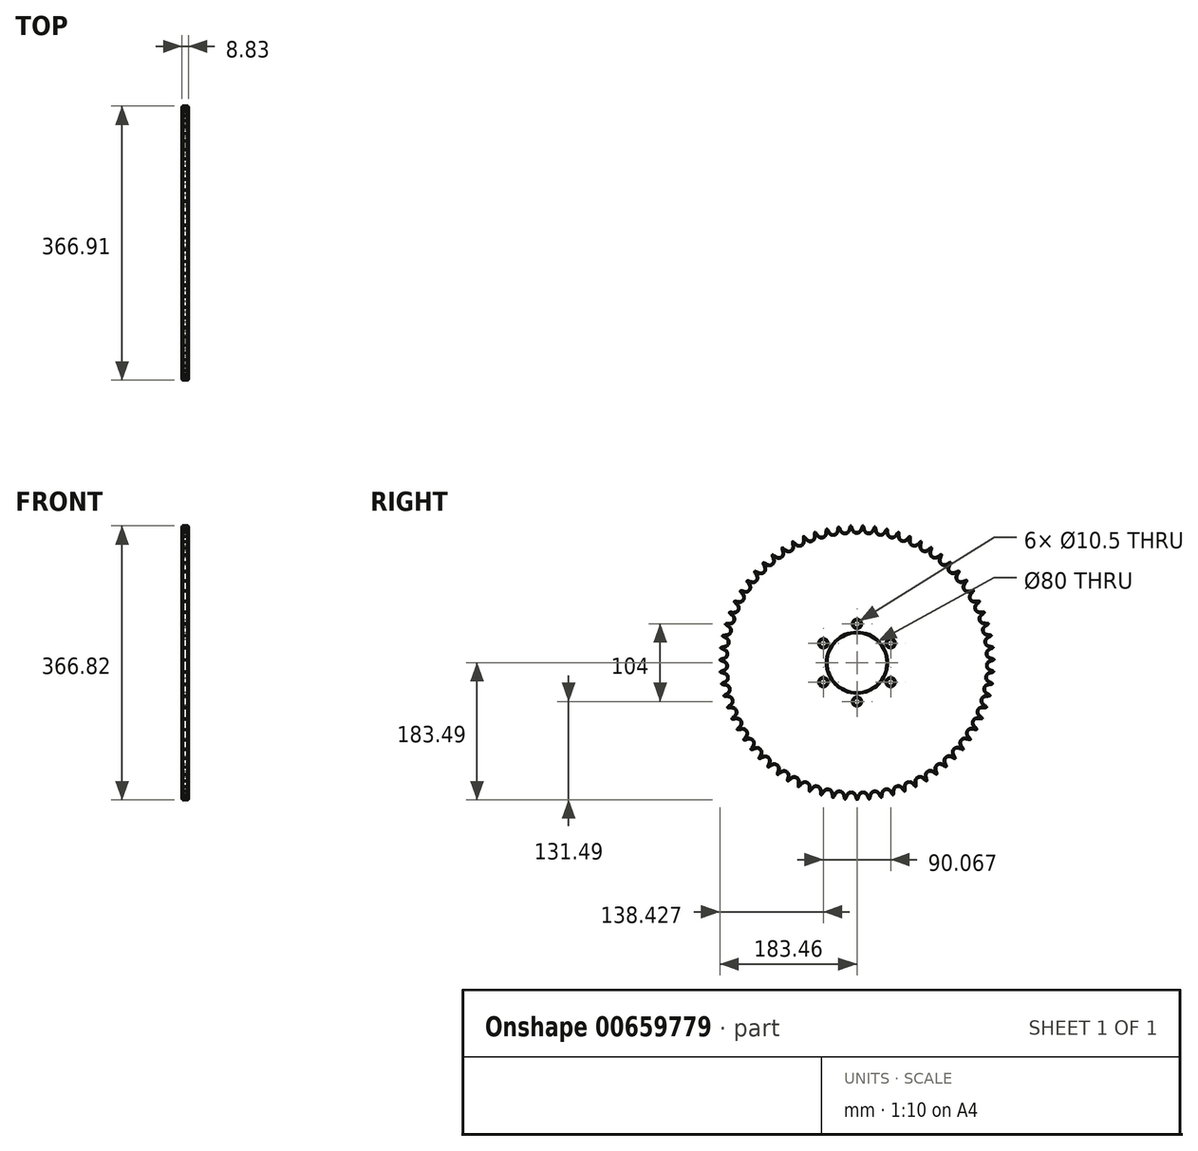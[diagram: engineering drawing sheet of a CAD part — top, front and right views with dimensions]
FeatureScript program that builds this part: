
annotation { "Feature Type Name" : "Feature", "Feature Type Description" : "" }
export const myFeature = defineFeature(function(context is Context, id is Id, definition is map)
    precondition{}
    {
        {
            var Q0;
            Q0=qCreatedBy(makeId("Front.planeOp"),FACE);
            var sketch = newSketch(context, id + "F0", { "sketchPlane" : qUnion([Q0])});
            skLineSegment(sketch, "E0", {"start": v(0, 0) * mm, "end": v(26.72, 0) * mm, "construction": true});
            skLineSegment(sketch, "E1.bottom", {"start": v(0, 40) * mm, "end": v(8.83, 40) * mm});
            skLineSegment(sketch, "E1.top", {"start": v(0, 183.5) * mm, "end": v(8.83, 183.5) * mm});
            skLineSegment(sketch, "E1.left", {"start": v(0, 40) * mm, "end": v(0, 183.5) * mm});
            skLineSegment(sketch, "E1.right", {"start": v(8.83, 40) * mm, "end": v(8.82, 183.5) * mm});
            skLineSegment(sketch, "E2.MirrorCS", {"start": v(8.83, -40) * mm, "end": v(8.83, -183.5) * mm});
            skLineSegment(sketch, "E3.MirrorCS", {"start": v(0, -183.5) * mm, "end": v(8.83, -183.5) * mm});
            skLineSegment(sketch, "E4.MirrorCS", {"start": v(0, -40) * mm, "end": v(8.83, -40) * mm});
            skLineSegment(sketch, "E5.MirrorCS", {"start": v(0, -40) * mm, "end": v(0, -183.5) * mm});
            skSolve(sketch);
        }
        {
            var Q0;
            Q0=makeQuery(id+"F0.imprint","IMPRINT",FACE,{"disambiguationData":[TD([[makeQuery(id+"F0.imprint","IMPRINT",EDGE,{"derivedFrom":sQuery(id+"F0.wireOp",EDGE,"E1.bottom")}),1.0]])]});
            var Q1;
            Q1=sQuery(id+"F0.wireOp",EDGE,"E0");
            revolve(context, id + "F1", {"entities" : qUnion([Q0]), "axis" : qUnion([Q1]), "revolveType" : RevolveType.FULL});
        }
        {
            var Q0;
            Q0=makeQuery(id+"F1.opRevolve","SWEPT_FACE",FACE,{"disambiguationData":[OSD([sQuery(id+"F0.wireOp",EDGE,"E1.left")])]});
            var sketch = newSketch(context, id + "F2", { "sketchPlane" : qUnion([Q0])});
            skCircle(sketch, "E6", {"center": v(0.24, 0) * mm, "radius": 183.5 * mm, "construction": true});
            skCircle(sketch, "E7", {"center": v(0.24, 0) * mm, "radius": 179.5 * mm, "construction": true});
            skCircle(sketch, "E8", {"center": v(0.24, 0) * mm, "radius": 174.3 * mm, "construction": true});
            skLineSegment(sketch, "E9", {"start": v(0.24, 0) * mm, "end": v(0.24, 107.73) * mm, "construction": true});
            skLineSegment(sketch, "E10", {"start": v(-3.61, 87) * mm, "end": v(0.24, 0) * mm, "construction": true});
            skLineSegment(sketch, "E11", {"start": v(0, 0) * mm, "end": v(0, 107.73) * mm, "construction": true});
            skLineSegment(sketch, "E12", {"start": v(0, 179.5) * mm, "end": v(-70.73, 128.4) * mm, "construction": true});
            skLineSegment(sketch, "E13", {"start": v(0, 179.5) * mm, "end": v(6.59, 184.25) * mm, "construction": true});
            skLineSegment(sketch, "E14", {"start": v(6.59, 184.25) * mm, "end": v(-48.15, 165.8) * mm, "construction": true});
            skLineSegment(sketch, "E15", {"start": v(-6, 180) * mm, "end": v(-6.35, 181.04) * mm});
            skLineSegment(sketch, "E16", {"start": v(-6.35, 181.04) * mm, "end": v(-12.59, 178.93) * mm, "construction": true});
            skArc(sketch, "E17", {"start": v(-6, 180) * mm, "mid": v(-5.22, 178.17) * mm, "end": v(-4.18, 176.47) * mm});
            skArc(sketch, "E18", {"start": v(-4.18, 176.47) * mm, "mid": v(18.4, 190.33) * mm, "end": v(-6, 180) * mm, "construction": true});
            skArc(sketch, "E19", {"start": v(0, 174.34) * mm, "mid": v(2.35, 184.08) * mm, "end": v(-4.18, 176.47) * mm, "construction": true});
            skArc(sketch, "E20", {"start": v(-4.18, 176.47) * mm, "mid": v(-2.35, 174.9) * mm, "end": v(0, 174.34) * mm});
            skLineSegment(sketch, "E21", {"start": v(0, 174.34) * mm, "end": v(0.24, 174.34) * mm});
            skArc(sketch, "E22", {"start": v(-7.89, 183.55) * mm, "mid": v(-18.2, 175.49) * mm, "end": v(-6.35, 181.04) * mm, "construction": true});
            skArc(sketch, "E23", {"start": v(-6.35, 181.04) * mm, "mid": v(-6.98, 182.38) * mm, "end": v(-7.89, 183.55) * mm});
            skArc(sketch, "E24.MirrorCS", {"start": v(4.65, 176.47) * mm, "mid": v(2.82, 174.9) * mm, "end": v(0.48, 174.34) * mm});
            skArc(sketch, "E25.MirrorCS", {"start": v(6.47, 180) * mm, "mid": v(5.7, 178.17) * mm, "end": v(4.65, 176.47) * mm});
            skLineSegment(sketch, "E26.MirrorCS", {"start": v(6.47, 180) * mm, "end": v(6.82, 181.04) * mm});
            skArc(sketch, "E27.MirrorCS", {"start": v(6.82, 181.04) * mm, "mid": v(7.45, 182.38) * mm, "end": v(8.36, 183.55) * mm});
            skLineSegment(sketch, "E28.MirrorCS", {"start": v(0.48, 174.34) * mm, "end": v(0.24, 174.34) * mm});
            skArc(sketch, "E29.1.0", {"start": v(-22.32, 179.77) * mm, "mid": v(-23.07, 181.05) * mm, "end": v(-24.08, 182.13) * mm});
            skArc(sketch, "E29.1.1", {"start": v(-9.2, 180.93) * mm, "mid": v(-8.7, 182.33) * mm, "end": v(-7.89, 183.57) * mm});
            skLineSegment(sketch, "E29.1.2", {"start": v(-9.46, 179.87) * mm, "end": v(-9.2, 180.93) * mm});
            skArc(sketch, "E29.1.3", {"start": v(-9.46, 179.87) * mm, "mid": v(-10.07, 177.98) * mm, "end": v(-10.96, 176.2) * mm});
            skArc(sketch, "E29.1.4", {"start": v(-10.96, 176.2) * mm, "mid": v(-12.65, 174.47) * mm, "end": v(-14.93, 173.7) * mm});
            skArc(sketch, "E29.1.5", {"start": v(-19.76, 175.41) * mm, "mid": v(-17.8, 174) * mm, "end": v(-15.4, 173.65) * mm});
            skArc(sketch, "E29.1.6", {"start": v(-21.88, 178.77) * mm, "mid": v(-20.95, 177.01) * mm, "end": v(-19.76, 175.41) * mm});
            skLineSegment(sketch, "E29.1.7", {"start": v(-21.88, 178.77) * mm, "end": v(-22.32, 179.77) * mm});
            skLineSegment(sketch, "E29.1.8", {"start": v(-14.93, 173.7) * mm, "end": v(-15.17, 173.67) * mm});
            skLineSegment(sketch, "E29.1.9", {"start": v(-15.4, 173.65) * mm, "end": v(-15.17, 173.67) * mm});
            skArc(sketch, "E29.2.0", {"start": v(-38.12, 177.1) * mm, "mid": v(-38.98, 178.3) * mm, "end": v(-40.08, 179.3) * mm});
            skArc(sketch, "E29.2.1", {"start": v(-25.16, 179.41) * mm, "mid": v(-24.78, 180.84) * mm, "end": v(-24.08, 182.15) * mm});
            skLineSegment(sketch, "E29.2.2", {"start": v(-25.32, 178.33) * mm, "end": v(-25.16, 179.41) * mm});
            skArc(sketch, "E29.2.3", {"start": v(-25.32, 178.33) * mm, "mid": v(-25.76, 176.4) * mm, "end": v(-26.49, 174.53) * mm});
            skArc(sketch, "E29.2.4", {"start": v(-26.49, 174.53) * mm, "mid": v(-28.02, 172.67) * mm, "end": v(-30.23, 171.7) * mm});
            skArc(sketch, "E29.2.5", {"start": v(-35.18, 172.98) * mm, "mid": v(-33.1, 171.76) * mm, "end": v(-30.7, 171.61) * mm});
            skArc(sketch, "E29.2.6", {"start": v(-37.6, 176.14) * mm, "mid": v(-36.51, 174.47) * mm, "end": v(-35.18, 172.98) * mm});
            skLineSegment(sketch, "E29.2.7", {"start": v(-37.6, 176.14) * mm, "end": v(-38.12, 177.1) * mm});
            skLineSegment(sketch, "E29.2.8", {"start": v(-30.23, 171.7) * mm, "end": v(-30.46, 171.65) * mm});
            skLineSegment(sketch, "E29.2.9", {"start": v(-30.7, 171.61) * mm, "end": v(-30.46, 171.65) * mm});
            skArc(sketch, "E29.3.0", {"start": v(-53.62, 173.03) * mm, "mid": v(-54.58, 174.16) * mm, "end": v(-55.77, 175.05) * mm});
            skArc(sketch, "E29.3.1", {"start": v(-40.92, 176.48) * mm, "mid": v(-40.66, 177.95) * mm, "end": v(-40.09, 179.31) * mm});
            skLineSegment(sketch, "E29.3.2", {"start": v(-40.98, 175.4) * mm, "end": v(-40.92, 176.48) * mm});
            skArc(sketch, "E29.3.3", {"start": v(-40.98, 175.4) * mm, "mid": v(-41.25, 173.42) * mm, "end": v(-41.81, 171.51) * mm});
            skArc(sketch, "E29.3.4", {"start": v(-41.81, 171.51) * mm, "mid": v(-43.17, 169.51) * mm, "end": v(-45.28, 168.35) * mm});
            skArc(sketch, "E29.3.5", {"start": v(-50.33, 169.2) * mm, "mid": v(-48.15, 168.16) * mm, "end": v(-45.74, 168.23) * mm});
            skArc(sketch, "E29.3.6", {"start": v(-53.02, 172.13) * mm, "mid": v(-51.79, 170.56) * mm, "end": v(-50.33, 169.2) * mm});
            skLineSegment(sketch, "E29.3.7", {"start": v(-53.02, 172.13) * mm, "end": v(-53.62, 173.03) * mm});
            skLineSegment(sketch, "E29.3.8", {"start": v(-45.28, 168.35) * mm, "end": v(-45.51, 168.3) * mm});
            skLineSegment(sketch, "E29.3.9", {"start": v(-45.74, 168.23) * mm, "end": v(-45.51, 168.3) * mm});
            skArc(sketch, "E29.4.0", {"start": v(-68.7, 167.61) * mm, "mid": v(-69.76, 168.66) * mm, "end": v(-71.02, 169.43) * mm});
            skArc(sketch, "E29.4.1", {"start": v(-56.36, 172.18) * mm, "mid": v(-56.23, 173.66) * mm, "end": v(-55.78, 175.07) * mm});
            skLineSegment(sketch, "E29.4.2", {"start": v(-56.32, 171.1) * mm, "end": v(-56.36, 172.18) * mm});
            skArc(sketch, "E29.4.3", {"start": v(-56.32, 171.1) * mm, "mid": v(-56.42, 169.1) * mm, "end": v(-56.8, 167.14) * mm});
            skArc(sketch, "E29.4.4", {"start": v(-56.8, 167.14) * mm, "mid": v(-57.98, 165.04) * mm, "end": v(-59.98, 163.7) * mm});
            skArc(sketch, "E29.4.5", {"start": v(-65.1, 164.08) * mm, "mid": v(-62.83, 163.24) * mm, "end": v(-60.43, 163.53) * mm});
            skArc(sketch, "E29.4.6", {"start": v(-68.02, 166.77) * mm, "mid": v(-66.66, 165.31) * mm, "end": v(-65.1, 164.08) * mm});
            skLineSegment(sketch, "E29.4.7", {"start": v(-68.02, 166.77) * mm, "end": v(-68.7, 167.61) * mm});
            skLineSegment(sketch, "E29.4.8", {"start": v(-59.98, 163.7) * mm, "end": v(-60.2, 163.6) * mm});
            skLineSegment(sketch, "E29.4.9", {"start": v(-60.43, 163.53) * mm, "end": v(-60.2, 163.6) * mm});
            skArc(sketch, "E29.5.0", {"start": v(-83.25, 160.89) * mm, "mid": v(-84.4, 161.83) * mm, "end": v(-85.72, 162.5) * mm});
            skArc(sketch, "E29.5.1", {"start": v(-71.35, 166.52) * mm, "mid": v(-71.36, 168) * mm, "end": v(-71.03, 169.45) * mm});
            skLineSegment(sketch, "E29.5.2", {"start": v(-71.22, 165.44) * mm, "end": v(-71.35, 166.52) * mm});
            skArc(sketch, "E29.5.3", {"start": v(-71.22, 165.44) * mm, "mid": v(-71.14, 163.45) * mm, "end": v(-71.36, 161.47) * mm});
            skArc(sketch, "E29.5.4", {"start": v(-71.36, 161.47) * mm, "mid": v(-72.34, 159.27) * mm, "end": v(-74.22, 157.75) * mm});
            skArc(sketch, "E29.5.5", {"start": v(-79.34, 157.69) * mm, "mid": v(-77, 157.05) * mm, "end": v(-74.65, 157.55) * mm});
            skArc(sketch, "E29.5.6", {"start": v(-82.5, 160.1) * mm, "mid": v(-81, 158.78) * mm, "end": v(-79.34, 157.69) * mm});
            skLineSegment(sketch, "E29.5.7", {"start": v(-82.5, 160.1) * mm, "end": v(-83.25, 160.89) * mm});
            skLineSegment(sketch, "E29.5.8", {"start": v(-74.22, 157.75) * mm, "end": v(-74.43, 157.65) * mm});
            skLineSegment(sketch, "E29.5.9", {"start": v(-74.65, 157.55) * mm, "end": v(-74.43, 157.65) * mm});
            skArc(sketch, "E29.6.0", {"start": v(-97.14, 152.9) * mm, "mid": v(-98.37, 153.74) * mm, "end": v(-99.75, 154.28) * mm});
            skArc(sketch, "E29.6.1", {"start": v(-85.79, 159.57) * mm, "mid": v(-85.93, 161.04) * mm, "end": v(-85.73, 162.51) * mm});
            skLineSegment(sketch, "E29.6.2", {"start": v(-85.57, 158.5) * mm, "end": v(-85.79, 159.57) * mm});
            skArc(sketch, "E29.6.3", {"start": v(-85.57, 158.5) * mm, "mid": v(-85.3, 156.52) * mm, "end": v(-85.35, 154.53) * mm});
            skArc(sketch, "E29.6.4", {"start": v(-85.35, 154.53) * mm, "mid": v(-86.13, 152.25) * mm, "end": v(-87.87, 150.57) * mm});
            skArc(sketch, "E29.6.5", {"start": v(-92.96, 150.06) * mm, "mid": v(-90.59, 149.63) * mm, "end": v(-88.28, 150.33) * mm});
            skArc(sketch, "E29.6.6", {"start": v(-96.32, 152.18) * mm, "mid": v(-94.72, 151) * mm, "end": v(-92.96, 150.06) * mm});
            skLineSegment(sketch, "E29.6.7", {"start": v(-96.32, 152.18) * mm, "end": v(-97.14, 152.9) * mm});
            skLineSegment(sketch, "E29.6.8", {"start": v(-87.87, 150.57) * mm, "end": v(-88.07, 150.45) * mm});
            skLineSegment(sketch, "E29.6.9", {"start": v(-88.28, 150.33) * mm, "end": v(-88.07, 150.45) * mm});
            skArc(sketch, "E29.7.0", {"start": v(-110.28, 143.71) * mm, "mid": v(-111.57, 144.44) * mm, "end": v(-113, 144.86) * mm});
            skArc(sketch, "E29.7.1", {"start": v(-99.56, 151.36) * mm, "mid": v(-99.82, 152.82) * mm, "end": v(-99.76, 154.3) * mm});
            skLineSegment(sketch, "E29.7.2", {"start": v(-99.24, 150.32) * mm, "end": v(-99.56, 151.36) * mm});
            skArc(sketch, "E29.7.3", {"start": v(-99.24, 150.32) * mm, "mid": v(-98.8, 148.37) * mm, "end": v(-98.67, 146.38) * mm});
            skArc(sketch, "E29.7.4", {"start": v(-98.67, 146.38) * mm, "mid": v(-99.25, 144.04) * mm, "end": v(-100.83, 142.22) * mm});
            skArc(sketch, "E29.7.5", {"start": v(-105.86, 141.26) * mm, "mid": v(-103.46, 141.04) * mm, "end": v(-101.22, 141.94) * mm});
            skArc(sketch, "E29.7.6", {"start": v(-109.4, 143.08) * mm, "mid": v(-107.7, 142.03) * mm, "end": v(-105.86, 141.26) * mm});
            skLineSegment(sketch, "E29.7.7", {"start": v(-109.4, 143.08) * mm, "end": v(-110.28, 143.71) * mm});
            skLineSegment(sketch, "E29.7.8", {"start": v(-100.83, 142.22) * mm, "end": v(-101.03, 142.08) * mm});
            skLineSegment(sketch, "E29.7.9", {"start": v(-101.22, 141.94) * mm, "end": v(-101.03, 142.08) * mm});
            skArc(sketch, "E29.8.0", {"start": v(-122.55, 133.4) * mm, "mid": v(-123.9, 134.02) * mm, "end": v(-125.35, 134.3) * mm});
            skArc(sketch, "E29.8.1", {"start": v(-112.54, 141.97) * mm, "mid": v(-112.94, 143.4) * mm, "end": v(-113, 144.88) * mm});
            skLineSegment(sketch, "E29.8.2", {"start": v(-112.14, 140.96) * mm, "end": v(-112.54, 141.97) * mm});
            skArc(sketch, "E29.8.3", {"start": v(-112.14, 140.96) * mm, "mid": v(-111.53, 139.06) * mm, "end": v(-111.22, 137.1) * mm});
            skArc(sketch, "E29.8.4", {"start": v(-111.22, 137.1) * mm, "mid": v(-111.6, 134.7) * mm, "end": v(-113, 132.75) * mm});
            skArc(sketch, "E29.8.5", {"start": v(-117.93, 131.35) * mm, "mid": v(-115.52, 131.34) * mm, "end": v(-113.37, 132.44) * mm});
            skArc(sketch, "E29.8.6", {"start": v(-121.61, 132.85) * mm, "mid": v(-119.83, 131.96) * mm, "end": v(-117.93, 131.35) * mm});
            skLineSegment(sketch, "E29.8.7", {"start": v(-121.61, 132.85) * mm, "end": v(-122.55, 133.4) * mm});
            skLineSegment(sketch, "E29.8.8", {"start": v(-113, 132.75) * mm, "end": v(-113.19, 132.6) * mm});
            skLineSegment(sketch, "E29.8.9", {"start": v(-113.37, 132.44) * mm, "end": v(-113.19, 132.6) * mm});
            skArc(sketch, "E29.9.0", {"start": v(-133.86, 122.05) * mm, "mid": v(-135.26, 122.54) * mm, "end": v(-136.73, 122.7) * mm});
            skArc(sketch, "E29.9.1", {"start": v(-124.65, 131.47) * mm, "mid": v(-125.17, 132.85) * mm, "end": v(-125.37, 134.33) * mm});
            skLineSegment(sketch, "E29.9.2", {"start": v(-124.16, 130.5) * mm, "end": v(-124.65, 131.47) * mm});
            skArc(sketch, "E29.9.3", {"start": v(-124.16, 130.5) * mm, "mid": v(-123.39, 128.66) * mm, "end": v(-122.9, 126.72) * mm});
            skArc(sketch, "E29.9.4", {"start": v(-122.9, 126.72) * mm, "mid": v(-123.06, 124.32) * mm, "end": v(-124.3, 122.24) * mm});
            skArc(sketch, "E29.9.5", {"start": v(-129.08, 120.4) * mm, "mid": v(-126.67, 120.62) * mm, "end": v(-124.63, 121.9) * mm});
            skArc(sketch, "E29.9.6", {"start": v(-132.88, 121.58) * mm, "mid": v(-131.02, 120.85) * mm, "end": v(-129.08, 120.4) * mm});
            skLineSegment(sketch, "E29.9.7", {"start": v(-132.88, 121.58) * mm, "end": v(-133.86, 122.05) * mm});
            skLineSegment(sketch, "E29.9.8", {"start": v(-124.3, 122.24) * mm, "end": v(-124.46, 122.07) * mm});
            skLineSegment(sketch, "E29.9.9", {"start": v(-124.63, 121.9) * mm, "end": v(-124.46, 122.07) * mm});
            skArc(sketch, "E29.10.0", {"start": v(-144.12, 109.74) * mm, "mid": v(-145.56, 110.1) * mm, "end": v(-147.04, 110.14) * mm});
            skArc(sketch, "E29.10.1", {"start": v(-135.78, 119.93) * mm, "mid": v(-136.42, 121.27) * mm, "end": v(-136.75, 122.72) * mm});
            skLineSegment(sketch, "E29.10.2", {"start": v(-135.2, 119.01) * mm, "end": v(-135.78, 119.93) * mm});
            skArc(sketch, "E29.10.3", {"start": v(-135.2, 119.01) * mm, "mid": v(-134.28, 117.25) * mm, "end": v(-133.62, 115.37) * mm});
            skArc(sketch, "E29.10.4", {"start": v(-133.62, 115.37) * mm, "mid": v(-133.57, 112.95) * mm, "end": v(-134.61, 110.78) * mm});
            skArc(sketch, "E29.10.5", {"start": v(-139.22, 108.53) * mm, "mid": v(-136.84, 108.95) * mm, "end": v(-134.92, 110.41) * mm});
            skArc(sketch, "E29.10.6", {"start": v(-143.1, 109.36) * mm, "mid": v(-141.2, 108.8) * mm, "end": v(-139.22, 108.53) * mm});
            skLineSegment(sketch, "E29.10.7", {"start": v(-143.1, 109.36) * mm, "end": v(-144.12, 109.74) * mm});
            skLineSegment(sketch, "E29.10.8", {"start": v(-134.61, 110.78) * mm, "end": v(-134.77, 110.6) * mm});
            skLineSegment(sketch, "E29.10.9", {"start": v(-134.92, 110.41) * mm, "end": v(-134.77, 110.6) * mm});
            skArc(sketch, "E29.11.0", {"start": v(-153.26, 96.58) * mm, "mid": v(-154.72, 96.81) * mm, "end": v(-156.2, 96.71) * mm});
            skArc(sketch, "E29.11.1", {"start": v(-145.85, 107.46) * mm, "mid": v(-146.6, 108.74) * mm, "end": v(-147.06, 110.15) * mm});
            skLineSegment(sketch, "E29.11.2", {"start": v(-145.2, 106.6) * mm, "end": v(-145.85, 107.46) * mm});
            skArc(sketch, "E29.11.3", {"start": v(-145.2, 106.6) * mm, "mid": v(-144.11, 104.92) * mm, "end": v(-143.3, 103.1) * mm});
            skArc(sketch, "E29.11.4", {"start": v(-143.3, 103.1) * mm, "mid": v(-143.03, 100.7) * mm, "end": v(-143.88, 98.45) * mm});
            skArc(sketch, "E29.11.5", {"start": v(-148.26, 95.8) * mm, "mid": v(-145.93, 96.43) * mm, "end": v(-144.15, 98.06) * mm});
            skArc(sketch, "E29.11.6", {"start": v(-152.2, 96.29) * mm, "mid": v(-150.25, 95.9) * mm, "end": v(-148.26, 95.8) * mm});
            skLineSegment(sketch, "E29.11.7", {"start": v(-152.2, 96.29) * mm, "end": v(-153.26, 96.58) * mm});
            skLineSegment(sketch, "E29.11.8", {"start": v(-143.88, 98.45) * mm, "end": v(-144.01, 98.25) * mm});
            skLineSegment(sketch, "E29.11.9", {"start": v(-144.15, 98.06) * mm, "end": v(-144.01, 98.25) * mm});
            skArc(sketch, "E29.12.0", {"start": v(-161.2, 82.65) * mm, "mid": v(-162.67, 82.76) * mm, "end": v(-164.14, 82.53) * mm});
            skArc(sketch, "E29.12.1", {"start": v(-154.78, 94.15) * mm, "mid": v(-155.64, 95.36) * mm, "end": v(-156.22, 96.73) * mm});
            skLineSegment(sketch, "E29.12.2", {"start": v(-154.05, 93.35) * mm, "end": v(-154.78, 94.15) * mm});
            skArc(sketch, "E29.12.3", {"start": v(-154.05, 93.35) * mm, "mid": v(-152.82, 91.78) * mm, "end": v(-151.85, 90.04) * mm});
            skArc(sketch, "E29.12.4", {"start": v(-151.85, 90.04) * mm, "mid": v(-151.37, 87.67) * mm, "end": v(-152.02, 85.35) * mm});
            skArc(sketch, "E29.12.5", {"start": v(-156.15, 82.32) * mm, "mid": v(-153.89, 83.16) * mm, "end": v(-152.25, 84.93) * mm});
            skArc(sketch, "E29.12.6", {"start": v(-160.12, 82.46) * mm, "mid": v(-158.14, 82.24) * mm, "end": v(-156.15, 82.32) * mm});
            skLineSegment(sketch, "E29.12.7", {"start": v(-160.12, 82.46) * mm, "end": v(-161.2, 82.65) * mm});
            skLineSegment(sketch, "E29.12.8", {"start": v(-152.02, 85.35) * mm, "end": v(-152.13, 85.14) * mm});
            skLineSegment(sketch, "E29.12.9", {"start": v(-152.25, 84.93) * mm, "end": v(-152.13, 85.14) * mm});
            skArc(sketch, "E29.13.0", {"start": v(-167.87, 68.09) * mm, "mid": v(-169.35, 68.06) * mm, "end": v(-170.79, 67.7) * mm});
            skArc(sketch, "E29.13.1", {"start": v(-162.5, 80.1) * mm, "mid": v(-163.46, 81.23) * mm, "end": v(-164.16, 82.54) * mm});
            skLineSegment(sketch, "E29.13.2", {"start": v(-161.7, 79.37) * mm, "end": v(-162.5, 80.1) * mm});
            skArc(sketch, "E29.13.3", {"start": v(-161.7, 79.37) * mm, "mid": v(-160.34, 77.9) * mm, "end": v(-159.2, 76.26) * mm});
            skArc(sketch, "E29.13.4", {"start": v(-159.2, 76.26) * mm, "mid": v(-158.52, 73.95) * mm, "end": v(-158.96, 71.58) * mm});
            skArc(sketch, "E29.13.5", {"start": v(-162.81, 68.2) * mm, "mid": v(-160.63, 69.23) * mm, "end": v(-159.16, 71.14) * mm});
            skArc(sketch, "E29.13.6", {"start": v(-166.78, 67.98) * mm, "mid": v(-164.8, 67.94) * mm, "end": v(-162.81, 68.2) * mm});
            skLineSegment(sketch, "E29.13.7", {"start": v(-166.78, 67.98) * mm, "end": v(-167.87, 68.09) * mm});
            skLineSegment(sketch, "E29.13.8", {"start": v(-158.96, 71.58) * mm, "end": v(-159.06, 71.36) * mm});
            skLineSegment(sketch, "E29.13.9", {"start": v(-159.16, 71.14) * mm, "end": v(-159.06, 71.36) * mm});
            skArc(sketch, "E29.14.0", {"start": v(-173.23, 52.98) * mm, "mid": v(-174.7, 52.83) * mm, "end": v(-176.1, 52.34) * mm});
            skArc(sketch, "E29.14.1", {"start": v(-168.94, 65.43) * mm, "mid": v(-170, 66.46) * mm, "end": v(-170.8, 67.7) * mm});
            skLineSegment(sketch, "E29.14.2", {"start": v(-168.08, 64.77) * mm, "end": v(-168.94, 65.43) * mm});
            skArc(sketch, "E29.14.3", {"start": v(-168.08, 64.77) * mm, "mid": v(-166.6, 63.43) * mm, "end": v(-165.33, 61.9) * mm});
            skArc(sketch, "E29.14.4", {"start": v(-165.33, 61.9) * mm, "mid": v(-164.44, 59.65) * mm, "end": v(-164.67, 57.25) * mm});
            skArc(sketch, "E29.14.5", {"start": v(-168.2, 53.54) * mm, "mid": v(-166.12, 54.76) * mm, "end": v(-164.82, 56.8) * mm});
            skArc(sketch, "E29.14.6", {"start": v(-172.14, 52.98) * mm, "mid": v(-170.15, 53.11) * mm, "end": v(-168.2, 53.54) * mm});
            skLineSegment(sketch, "E29.14.7", {"start": v(-172.14, 52.98) * mm, "end": v(-173.23, 52.98) * mm});
            skLineSegment(sketch, "E29.14.8", {"start": v(-164.67, 57.25) * mm, "end": v(-164.75, 57.02) * mm});
            skLineSegment(sketch, "E29.14.9", {"start": v(-164.82, 56.8) * mm, "end": v(-164.75, 57.02) * mm});
            skArc(sketch, "E29.15.0", {"start": v(-177.23, 37.47) * mm, "mid": v(-178.69, 37.18) * mm, "end": v(-180.04, 36.57) * mm});
            skArc(sketch, "E29.15.1", {"start": v(-174.06, 50.24) * mm, "mid": v(-175.21, 51.18) * mm, "end": v(-176.12, 52.35) * mm});
            skLineSegment(sketch, "E29.15.2", {"start": v(-173.14, 49.66) * mm, "end": v(-174.06, 50.24) * mm});
            skArc(sketch, "E29.15.3", {"start": v(-173.14, 49.66) * mm, "mid": v(-171.55, 48.46) * mm, "end": v(-170.15, 47.04) * mm});
            skArc(sketch, "E29.15.4", {"start": v(-170.15, 47.04) * mm, "mid": v(-169.07, 44.88) * mm, "end": v(-169.08, 42.47) * mm});
            skArc(sketch, "E29.15.5", {"start": v(-172.28, 38.47) * mm, "mid": v(-170.31, 39.87) * mm, "end": v(-169.2, 42) * mm});
            skArc(sketch, "E29.15.6", {"start": v(-176.15, 37.55) * mm, "mid": v(-174.18, 37.87) * mm, "end": v(-172.28, 38.47) * mm});
            skLineSegment(sketch, "E29.15.7", {"start": v(-176.15, 37.55) * mm, "end": v(-177.23, 37.47) * mm});
            skLineSegment(sketch, "E29.15.8", {"start": v(-169.08, 42.47) * mm, "end": v(-169.14, 42.24) * mm});
            skLineSegment(sketch, "E29.15.9", {"start": v(-169.2, 42) * mm, "end": v(-169.14, 42.24) * mm});
            skArc(sketch, "E29.16.0", {"start": v(-179.85, 21.66) * mm, "mid": v(-181.27, 21.24) * mm, "end": v(-182.57, 20.52) * mm});
            skArc(sketch, "E29.16.1", {"start": v(-177.82, 34.66) * mm, "mid": v(-179.05, 35.5) * mm, "end": v(-180.06, 36.58) * mm});
            skLineSegment(sketch, "E29.16.2", {"start": v(-176.85, 34.16) * mm, "end": v(-177.82, 34.66) * mm});
            skArc(sketch, "E29.16.3", {"start": v(-176.85, 34.16) * mm, "mid": v(-175.16, 33.11) * mm, "end": v(-173.64, 31.82) * mm});
            skArc(sketch, "E29.16.4", {"start": v(-173.64, 31.82) * mm, "mid": v(-172.37, 29.77) * mm, "end": v(-172.18, 27.36) * mm});
            skArc(sketch, "E29.16.5", {"start": v(-175, 23.1) * mm, "mid": v(-173.17, 24.66) * mm, "end": v(-172.25, 26.9) * mm});
            skArc(sketch, "E29.16.6", {"start": v(-178.78, 21.84) * mm, "mid": v(-176.84, 22.32) * mm, "end": v(-175, 23.1) * mm});
            skLineSegment(sketch, "E29.16.7", {"start": v(-178.78, 21.84) * mm, "end": v(-179.85, 21.66) * mm});
            skLineSegment(sketch, "E29.16.8", {"start": v(-172.18, 27.36) * mm, "end": v(-172.21, 27.13) * mm});
            skLineSegment(sketch, "E29.16.9", {"start": v(-172.25, 26.9) * mm, "end": v(-172.21, 27.13) * mm});
            skArc(sketch, "E29.17.0", {"start": v(-181.06, 5.68) * mm, "mid": v(-182.44, 5.14) * mm, "end": v(-183.67, 4.3) * mm});
            skArc(sketch, "E29.17.1", {"start": v(-180.19, 18.81) * mm, "mid": v(-181.48, 19.53) * mm, "end": v(-182.6, 20.52) * mm});
            skLineSegment(sketch, "E29.17.2", {"start": v(-179.18, 18.4) * mm, "end": v(-180.19, 18.81) * mm});
            skArc(sketch, "E29.17.3", {"start": v(-179.18, 18.4) * mm, "mid": v(-177.4, 17.5) * mm, "end": v(-175.77, 16.35) * mm});
            skArc(sketch, "E29.17.4", {"start": v(-175.77, 16.35) * mm, "mid": v(-174.33, 14.42) * mm, "end": v(-173.92, 12.04) * mm});
            skArc(sketch, "E29.17.5", {"start": v(-176.36, 7.53) * mm, "mid": v(-174.67, 9.26) * mm, "end": v(-173.95, 11.56) * mm});
            skArc(sketch, "E29.17.6", {"start": v(-180, 5.95) * mm, "mid": v(-178.12, 6.6) * mm, "end": v(-176.36, 7.53) * mm});
            skLineSegment(sketch, "E29.17.7", {"start": v(-180, 5.95) * mm, "end": v(-181.06, 5.68) * mm});
            skLineSegment(sketch, "E29.17.8", {"start": v(-173.92, 12.04) * mm, "end": v(-173.94, 11.8) * mm});
            skLineSegment(sketch, "E29.17.9", {"start": v(-173.95, 11.56) * mm, "end": v(-173.94, 11.8) * mm});
            skArc(sketch, "E29.18.0", {"start": v(-180.85, -10.35) * mm, "mid": v(-182.18, -11) * mm, "end": v(-183.33, -11.95) * mm});
            skArc(sketch, "E29.18.1", {"start": v(-181.14, 2.82) * mm, "mid": v(-182.5, 3.41) * mm, "end": v(-183.69, 4.3) * mm});
            skLineSegment(sketch, "E29.18.2", {"start": v(-180.1, 2.5) * mm, "end": v(-181.14, 2.82) * mm});
            skArc(sketch, "E29.18.3", {"start": v(-180.1, 2.5) * mm, "mid": v(-178.25, 1.75) * mm, "end": v(-176.53, 0.75) * mm});
            skArc(sketch, "E29.18.4", {"start": v(-176.53, 0.75) * mm, "mid": v(-174.92, -1.05) * mm, "end": v(-174.3, -3.38) * mm});
            skArc(sketch, "E29.18.5", {"start": v(-176.34, -8.08) * mm, "mid": v(-174.8, -6.22) * mm, "end": v(-174.3, -3.86) * mm});
            skArc(sketch, "E29.18.6", {"start": v(-179.83, -9.98) * mm, "mid": v(-178.01, -9.16) * mm, "end": v(-176.34, -8.08) * mm});
            skLineSegment(sketch, "E29.18.7", {"start": v(-179.83, -9.98) * mm, "end": v(-180.85, -10.35) * mm});
            skLineSegment(sketch, "E29.18.8", {"start": v(-174.3, -3.38) * mm, "end": v(-174.3, -3.62) * mm});
            skLineSegment(sketch, "E29.18.9", {"start": v(-174.3, -3.86) * mm, "end": v(-174.3, -3.62) * mm});
            skArc(sketch, "E29.19.0", {"start": v(-179.23, -26.3) * mm, "mid": v(-180.5, -27.07) * mm, "end": v(-181.56, -28.1) * mm});
            skArc(sketch, "E29.19.1", {"start": v(-180.68, -13.2) * mm, "mid": v(-182.09, -12.73) * mm, "end": v(-183.35, -11.95) * mm});
            skLineSegment(sketch, "E29.19.2", {"start": v(-179.62, -13.44) * mm, "end": v(-180.68, -13.2) * mm});
            skArc(sketch, "E29.19.3", {"start": v(-179.62, -13.44) * mm, "mid": v(-177.71, -14) * mm, "end": v(-175.9, -14.86) * mm});
            skArc(sketch, "E29.19.4", {"start": v(-175.9, -14.86) * mm, "mid": v(-174.14, -16.5) * mm, "end": v(-173.32, -18.77) * mm});
            skArc(sketch, "E29.19.5", {"start": v(-174.93, -23.63) * mm, "mid": v(-173.57, -21.64) * mm, "end": v(-173.27, -19.25) * mm});
            skArc(sketch, "E29.19.6", {"start": v(-178.24, -25.83) * mm, "mid": v(-176.5, -24.86) * mm, "end": v(-174.93, -23.63) * mm});
            skLineSegment(sketch, "E29.19.7", {"start": v(-178.24, -25.83) * mm, "end": v(-179.23, -26.3) * mm});
            skLineSegment(sketch, "E29.19.8", {"start": v(-173.32, -18.77) * mm, "end": v(-173.3, -19) * mm});
            skLineSegment(sketch, "E29.19.9", {"start": v(-173.27, -19.25) * mm, "end": v(-173.3, -19) * mm});
            skArc(sketch, "E29.20.0", {"start": v(-176.2, -42.03) * mm, "mid": v(-177.4, -42.91) * mm, "end": v(-178.36, -44.04) * mm});
            skArc(sketch, "E29.20.1", {"start": v(-178.8, -29.12) * mm, "mid": v(-180.25, -28.77) * mm, "end": v(-181.58, -28.1) * mm});
            skLineSegment(sketch, "E29.20.2", {"start": v(-177.73, -29.26) * mm, "end": v(-178.8, -29.12) * mm});
            skArc(sketch, "E29.20.3", {"start": v(-177.73, -29.26) * mm, "mid": v(-175.78, -29.66) * mm, "end": v(-173.9, -30.34) * mm});
            skArc(sketch, "E29.20.4", {"start": v(-173.9, -30.34) * mm, "mid": v(-172, -31.83) * mm, "end": v(-170.99, -34.02) * mm});
            skArc(sketch, "E29.20.5", {"start": v(-172.16, -39) * mm, "mid": v(-170.98, -36.9) * mm, "end": v(-170.9, -34.48) * mm});
            skArc(sketch, "E29.20.6", {"start": v(-175.26, -41.49) * mm, "mid": v(-173.62, -40.36) * mm, "end": v(-172.16, -39) * mm});
            skLineSegment(sketch, "E29.20.7", {"start": v(-175.26, -41.49) * mm, "end": v(-176.2, -42.03) * mm});
            skLineSegment(sketch, "E29.20.8", {"start": v(-170.99, -34.02) * mm, "end": v(-170.94, -34.25) * mm});
            skLineSegment(sketch, "E29.20.9", {"start": v(-170.9, -34.48) * mm, "end": v(-170.94, -34.25) * mm});
            skArc(sketch, "E29.21.0", {"start": v(-171.8, -57.44) * mm, "mid": v(-172.91, -58.42) * mm, "end": v(-173.77, -59.63) * mm});
            skArc(sketch, "E29.21.1", {"start": v(-175.54, -44.81) * mm, "mid": v(-177, -44.59) * mm, "end": v(-178.38, -44.04) * mm});
            skLineSegment(sketch, "E29.21.2", {"start": v(-174.45, -44.85) * mm, "end": v(-175.54, -44.81) * mm});
            skArc(sketch, "E29.21.3", {"start": v(-174.45, -44.85) * mm, "mid": v(-172.47, -45.08) * mm, "end": v(-170.54, -45.6) * mm});
            skArc(sketch, "E29.21.4", {"start": v(-170.54, -45.6) * mm, "mid": v(-168.52, -46.9) * mm, "end": v(-167.3, -49) * mm});
            skArc(sketch, "E29.21.5", {"start": v(-168.04, -54.07) * mm, "mid": v(-167.05, -51.86) * mm, "end": v(-167.17, -49.45) * mm});
            skArc(sketch, "E29.21.6", {"start": v(-170.91, -56.81) * mm, "mid": v(-169.37, -55.55) * mm, "end": v(-168.04, -54.07) * mm});
            skLineSegment(sketch, "E29.21.7", {"start": v(-170.91, -56.81) * mm, "end": v(-171.8, -57.44) * mm});
            skLineSegment(sketch, "E29.21.8", {"start": v(-167.3, -49) * mm, "end": v(-167.24, -49.22) * mm});
            skLineSegment(sketch, "E29.21.9", {"start": v(-167.17, -49.45) * mm, "end": v(-167.24, -49.22) * mm});
            skArc(sketch, "E29.22.0", {"start": v(-166.05, -72.4) * mm, "mid": v(-167.07, -73.48) * mm, "end": v(-167.82, -74.76) * mm});
            skArc(sketch, "E29.22.1", {"start": v(-170.89, -60.15) * mm, "mid": v(-172.37, -60.06) * mm, "end": v(-173.8, -59.64) * mm});
            skLineSegment(sketch, "E29.22.2", {"start": v(-169.8, -60.1) * mm, "end": v(-170.89, -60.15) * mm});
            skArc(sketch, "E29.22.3", {"start": v(-169.8, -60.1) * mm, "mid": v(-167.8, -60.14) * mm, "end": v(-165.85, -60.49) * mm});
            skArc(sketch, "E29.22.4", {"start": v(-165.85, -60.49) * mm, "mid": v(-163.71, -61.62) * mm, "end": v(-162.32, -63.6) * mm});
            skArc(sketch, "E29.22.5", {"start": v(-162.6, -68.7) * mm, "mid": v(-161.81, -66.42) * mm, "end": v(-162.15, -64.03) * mm});
            skArc(sketch, "E29.22.6", {"start": v(-165.22, -71.7) * mm, "mid": v(-163.8, -70.3) * mm, "end": v(-162.6, -68.7) * mm});
            skLineSegment(sketch, "E29.22.7", {"start": v(-165.22, -71.7) * mm, "end": v(-166.05, -72.4) * mm});
            skLineSegment(sketch, "E29.22.8", {"start": v(-162.32, -63.6) * mm, "end": v(-162.24, -63.81) * mm});
            skLineSegment(sketch, "E29.22.9", {"start": v(-162.15, -64.03) * mm, "end": v(-162.24, -63.81) * mm});
            skArc(sketch, "E29.23.0", {"start": v(-159, -86.79) * mm, "mid": v(-159.92, -87.95) * mm, "end": v(-160.56, -89.3) * mm});
            skArc(sketch, "E29.23.1", {"start": v(-164.9, -75.02) * mm, "mid": v(-166.39, -75.06) * mm, "end": v(-167.84, -74.76) * mm});
            skLineSegment(sketch, "E29.23.2", {"start": v(-163.83, -74.87) * mm, "end": v(-164.9, -75.02) * mm});
            skArc(sketch, "E29.23.3", {"start": v(-163.83, -74.87) * mm, "mid": v(-161.84, -74.74) * mm, "end": v(-159.85, -74.91) * mm});
            skArc(sketch, "E29.23.4", {"start": v(-159.85, -74.91) * mm, "mid": v(-157.63, -75.84) * mm, "end": v(-156.07, -77.69) * mm});
            skArc(sketch, "E29.23.5", {"start": v(-155.9, -82.8) * mm, "mid": v(-155.3, -80.47) * mm, "end": v(-155.86, -78.11) * mm});
            skArc(sketch, "E29.23.6", {"start": v(-158.24, -86.02) * mm, "mid": v(-156.95, -84.5) * mm, "end": v(-155.9, -82.8) * mm});
            skLineSegment(sketch, "E29.23.7", {"start": v(-158.24, -86.02) * mm, "end": v(-159, -86.79) * mm});
            skLineSegment(sketch, "E29.23.8", {"start": v(-156.07, -77.69) * mm, "end": v(-155.96, -77.9) * mm});
            skLineSegment(sketch, "E29.23.9", {"start": v(-155.86, -78.11) * mm, "end": v(-155.96, -77.9) * mm});
            skArc(sketch, "E29.24.0", {"start": v(-150.71, -100.5) * mm, "mid": v(-151.52, -101.74) * mm, "end": v(-152.04, -103.14) * mm});
            skArc(sketch, "E29.24.1", {"start": v(-157.63, -89.3) * mm, "mid": v(-159.1, -89.47) * mm, "end": v(-160.58, -89.3) * mm});
            skLineSegment(sketch, "E29.24.2", {"start": v(-156.57, -89.05) * mm, "end": v(-157.63, -89.3) * mm});
            skArc(sketch, "E29.24.3", {"start": v(-156.57, -89.05) * mm, "mid": v(-154.6, -88.75) * mm, "end": v(-152.6, -88.74) * mm});
            skArc(sketch, "E29.24.4", {"start": v(-152.6, -88.74) * mm, "mid": v(-150.3, -89.48) * mm, "end": v(-148.6, -91.18) * mm});
            skArc(sketch, "E29.24.5", {"start": v(-147.97, -96.26) * mm, "mid": v(-147.6, -93.88) * mm, "end": v(-148.34, -91.58) * mm});
            skArc(sketch, "E29.24.6", {"start": v(-150.02, -99.67) * mm, "mid": v(-148.86, -98.04) * mm, "end": v(-147.97, -96.26) * mm});
            skLineSegment(sketch, "E29.24.7", {"start": v(-150.02, -99.67) * mm, "end": v(-150.71, -100.5) * mm});
            skLineSegment(sketch, "E29.24.8", {"start": v(-148.6, -91.18) * mm, "end": v(-148.47, -91.38) * mm});
            skLineSegment(sketch, "E29.24.9", {"start": v(-148.34, -91.58) * mm, "end": v(-148.47, -91.38) * mm});
            skArc(sketch, "E29.25.0", {"start": v(-141.24, -113.43) * mm, "mid": v(-141.94, -114.74) * mm, "end": v(-142.33, -116.17) * mm});
            skArc(sketch, "E29.25.1", {"start": v(-149.12, -102.88) * mm, "mid": v(-150.57, -103.18) * mm, "end": v(-152.06, -103.15) * mm});
            skLineSegment(sketch, "E29.25.2", {"start": v(-148.09, -102.54) * mm, "end": v(-149.12, -102.88) * mm});
            skArc(sketch, "E29.25.3", {"start": v(-148.09, -102.54) * mm, "mid": v(-146.15, -102.07) * mm, "end": v(-144.17, -101.88) * mm});
            skArc(sketch, "E29.25.4", {"start": v(-144.17, -101.88) * mm, "mid": v(-141.8, -102.41) * mm, "end": v(-139.95, -103.95) * mm});
            skArc(sketch, "E29.25.5", {"start": v(-138.88, -108.96) * mm, "mid": v(-138.72, -106.55) * mm, "end": v(-139.67, -104.34) * mm});
            skArc(sketch, "E29.25.6", {"start": v(-140.62, -112.53) * mm, "mid": v(-139.62, -110.81) * mm, "end": v(-138.88, -108.96) * mm});
            skLineSegment(sketch, "E29.25.7", {"start": v(-140.62, -112.53) * mm, "end": v(-141.24, -113.43) * mm});
            skLineSegment(sketch, "E29.25.8", {"start": v(-139.95, -103.95) * mm, "end": v(-139.81, -104.14) * mm});
            skLineSegment(sketch, "E29.25.9", {"start": v(-139.67, -104.34) * mm, "end": v(-139.81, -104.14) * mm});
            skArc(sketch, "E29.26.0", {"start": v(-130.66, -125.47) * mm, "mid": v(-131.24, -126.83) * mm, "end": v(-131.5, -128.3) * mm});
            skArc(sketch, "E29.26.1", {"start": v(-139.44, -115.66) * mm, "mid": v(-140.86, -116.08) * mm, "end": v(-142.34, -116.18) * mm});
            skLineSegment(sketch, "E29.26.2", {"start": v(-138.44, -115.23) * mm, "end": v(-139.44, -115.66) * mm});
            skArc(sketch, "E29.26.3", {"start": v(-138.44, -115.23) * mm, "mid": v(-136.56, -114.58) * mm, "end": v(-134.6, -114.23) * mm});
            skArc(sketch, "E29.26.4", {"start": v(-134.6, -114.23) * mm, "mid": v(-132.2, -114.54) * mm, "end": v(-130.22, -115.92) * mm});
            skArc(sketch, "E29.26.5", {"start": v(-128.7, -120.8) * mm, "mid": v(-128.76, -118.4) * mm, "end": v(-129.9, -116.27) * mm});
            skArc(sketch, "E29.26.6", {"start": v(-130.13, -124.52) * mm, "mid": v(-129.28, -122.72) * mm, "end": v(-128.7, -120.8) * mm});
            skLineSegment(sketch, "E29.26.7", {"start": v(-130.13, -124.52) * mm, "end": v(-130.66, -125.47) * mm});
            skLineSegment(sketch, "E29.26.8", {"start": v(-130.22, -115.92) * mm, "end": v(-130.06, -116.1) * mm});
            skLineSegment(sketch, "E29.26.9", {"start": v(-129.9, -116.27) * mm, "end": v(-130.06, -116.1) * mm});
            skArc(sketch, "E29.27.0", {"start": v(-119.06, -136.53) * mm, "mid": v(-119.52, -137.94) * mm, "end": v(-119.65, -139.41) * mm});
            skArc(sketch, "E29.27.1", {"start": v(-128.68, -127.53) * mm, "mid": v(-130.05, -128.08) * mm, "end": v(-131.52, -128.3) * mm});
            skLineSegment(sketch, "E29.27.2", {"start": v(-127.72, -127.01) * mm, "end": v(-128.68, -127.53) * mm});
            skArc(sketch, "E29.27.3", {"start": v(-127.72, -127.01) * mm, "mid": v(-125.9, -126.2) * mm, "end": v(-123.97, -125.68) * mm});
            skArc(sketch, "E29.27.4", {"start": v(-123.97, -125.68) * mm, "mid": v(-121.56, -125.78) * mm, "end": v(-119.46, -126.97) * mm});
            skArc(sketch, "E29.27.5", {"start": v(-117.52, -131.71) * mm, "mid": v(-117.79, -129.31) * mm, "end": v(-119.12, -127.3) * mm});
            skArc(sketch, "E29.27.6", {"start": v(-118.61, -135.54) * mm, "mid": v(-117.92, -133.66) * mm, "end": v(-117.52, -131.71) * mm});
            skLineSegment(sketch, "E29.27.7", {"start": v(-118.61, -135.54) * mm, "end": v(-119.06, -136.53) * mm});
            skLineSegment(sketch, "E29.27.8", {"start": v(-119.46, -126.97) * mm, "end": v(-119.29, -127.13) * mm});
            skLineSegment(sketch, "E29.27.9", {"start": v(-119.12, -127.3) * mm, "end": v(-119.29, -127.13) * mm});
            skArc(sketch, "E29.28.0", {"start": v(-106.53, -146.51) * mm, "mid": v(-106.86, -147.96) * mm, "end": v(-106.86, -149.44) * mm});
            skArc(sketch, "E29.28.1", {"start": v(-116.9, -138.4) * mm, "mid": v(-118.22, -139.07) * mm, "end": v(-119.66, -139.43) * mm});
            skLineSegment(sketch, "E29.28.2", {"start": v(-116, -137.8) * mm, "end": v(-116.9, -138.4) * mm});
            skArc(sketch, "E29.28.3", {"start": v(-116, -137.8) * mm, "mid": v(-114.25, -136.84) * mm, "end": v(-112.38, -136.14) * mm});
            skArc(sketch, "E29.28.4", {"start": v(-112.38, -136.14) * mm, "mid": v(-109.97, -136.03) * mm, "end": v(-107.77, -137.03) * mm});
            skArc(sketch, "E29.28.5", {"start": v(-105.42, -141.58) * mm, "mid": v(-105.9, -139.22) * mm, "end": v(-107.4, -137.33) * mm});
            skArc(sketch, "E29.28.6", {"start": v(-106.17, -145.49) * mm, "mid": v(-105.65, -143.56) * mm, "end": v(-105.42, -141.58) * mm});
            skLineSegment(sketch, "E29.28.7", {"start": v(-106.17, -145.49) * mm, "end": v(-106.53, -146.51) * mm});
            skLineSegment(sketch, "E29.28.8", {"start": v(-107.77, -137.03) * mm, "end": v(-107.59, -137.18) * mm});
            skLineSegment(sketch, "E29.28.9", {"start": v(-107.4, -137.33) * mm, "end": v(-107.59, -137.18) * mm});
            skArc(sketch, "E29.29.0", {"start": v(-93.16, -155.36) * mm, "mid": v(-93.37, -156.83) * mm, "end": v(-93.23, -158.3) * mm});
            skArc(sketch, "E29.29.1", {"start": v(-104.21, -148.2) * mm, "mid": v(-105.47, -148.98) * mm, "end": v(-106.87, -149.46) * mm});
            skLineSegment(sketch, "E29.29.2", {"start": v(-103.36, -147.52) * mm, "end": v(-104.21, -148.2) * mm});
            skArc(sketch, "E29.29.3", {"start": v(-103.36, -147.52) * mm, "mid": v(-101.7, -146.4) * mm, "end": v(-99.91, -145.54) * mm});
            skArc(sketch, "E29.29.4", {"start": v(-99.91, -145.54) * mm, "mid": v(-97.52, -145.22) * mm, "end": v(-95.24, -146.02) * mm});
            skArc(sketch, "E29.29.5", {"start": v(-92.5, -150.35) * mm, "mid": v(-93.18, -148.03) * mm, "end": v(-94.84, -146.28) * mm});
            skArc(sketch, "E29.29.6", {"start": v(-92.9, -154.3) * mm, "mid": v(-92.55, -152.34) * mm, "end": v(-92.5, -150.35) * mm});
            skLineSegment(sketch, "E29.29.7", {"start": v(-92.9, -154.3) * mm, "end": v(-93.16, -155.36) * mm});
            skLineSegment(sketch, "E29.29.8", {"start": v(-95.24, -146.02) * mm, "end": v(-95.04, -146.15) * mm});
            skLineSegment(sketch, "E29.29.9", {"start": v(-94.84, -146.28) * mm, "end": v(-95.04, -146.15) * mm});
            skArc(sketch, "E29.30.0", {"start": v(-79.07, -162.98) * mm, "mid": v(-79.14, -164.46) * mm, "end": v(-78.88, -165.92) * mm});
            skArc(sketch, "E29.30.1", {"start": v(-90.7, -156.82) * mm, "mid": v(-91.9, -157.72) * mm, "end": v(-93.25, -158.32) * mm});
            skLineSegment(sketch, "E29.30.2", {"start": v(-89.92, -156.07) * mm, "end": v(-90.7, -156.82) * mm});
            skArc(sketch, "E29.30.3", {"start": v(-89.92, -156.07) * mm, "mid": v(-88.37, -154.81) * mm, "end": v(-86.66, -153.8) * mm});
            skArc(sketch, "E29.30.4", {"start": v(-86.66, -153.8) * mm, "mid": v(-84.3, -153.27) * mm, "end": v(-81.96, -153.87) * mm});
            skArc(sketch, "E29.30.5", {"start": v(-78.85, -157.93) * mm, "mid": v(-79.73, -155.69) * mm, "end": v(-81.54, -154.1) * mm});
            skArc(sketch, "E29.30.6", {"start": v(-78.9, -161.9) * mm, "mid": v(-78.72, -159.92) * mm, "end": v(-78.85, -157.93) * mm});
            skLineSegment(sketch, "E29.30.7", {"start": v(-78.9, -161.9) * mm, "end": v(-79.07, -162.98) * mm});
            skLineSegment(sketch, "E29.30.8", {"start": v(-81.96, -153.87) * mm, "end": v(-81.75, -153.98) * mm});
            skLineSegment(sketch, "E29.30.9", {"start": v(-81.54, -154.1) * mm, "end": v(-81.75, -153.98) * mm});
            skArc(sketch, "E29.31.0", {"start": v(-64.35, -169.33) * mm, "mid": v(-64.3, -170.81) * mm, "end": v(-63.9, -172.25) * mm});
            skArc(sketch, "E29.31.1", {"start": v(-76.5, -164.23) * mm, "mid": v(-77.6, -165.22) * mm, "end": v(-78.89, -165.94) * mm});
            skLineSegment(sketch, "E29.31.2", {"start": v(-75.77, -163.41) * mm, "end": v(-76.5, -164.23) * mm});
            skArc(sketch, "E29.31.3", {"start": v(-75.77, -163.41) * mm, "mid": v(-74.34, -162.02) * mm, "end": v(-72.72, -160.86) * mm});
            skArc(sketch, "E29.31.4", {"start": v(-72.72, -160.86) * mm, "mid": v(-70.43, -160.12) * mm, "end": v(-68.04, -160.5) * mm});
            skArc(sketch, "E29.31.5", {"start": v(-64.58, -164.28) * mm, "mid": v(-65.66, -162.12) * mm, "end": v(-67.6, -160.7) * mm});
            skArc(sketch, "E29.31.6", {"start": v(-64.28, -168.25) * mm, "mid": v(-64.28, -166.25) * mm, "end": v(-64.58, -164.28) * mm});
            skLineSegment(sketch, "E29.31.7", {"start": v(-64.28, -168.25) * mm, "end": v(-64.35, -169.33) * mm});
            skLineSegment(sketch, "E29.31.8", {"start": v(-68.04, -160.5) * mm, "end": v(-67.82, -160.6) * mm});
            skLineSegment(sketch, "E29.31.9", {"start": v(-67.6, -160.7) * mm, "end": v(-67.82, -160.6) * mm});
            skArc(sketch, "E29.32.0", {"start": v(-49.14, -174.36) * mm, "mid": v(-48.95, -175.83) * mm, "end": v(-48.43, -177.22) * mm});
            skArc(sketch, "E29.32.1", {"start": v(-61.68, -170.34) * mm, "mid": v(-62.69, -171.43) * mm, "end": v(-63.91, -172.27) * mm});
            skLineSegment(sketch, "E29.32.2", {"start": v(-61.03, -169.47) * mm, "end": v(-61.68, -170.34) * mm});
            skArc(sketch, "E29.32.3", {"start": v(-61.03, -169.47) * mm, "mid": v(-59.73, -167.96) * mm, "end": v(-58.22, -166.66) * mm});
            skArc(sketch, "E29.32.4", {"start": v(-58.22, -166.66) * mm, "mid": v(-56, -165.72) * mm, "end": v(-53.6, -165.9) * mm});
            skArc(sketch, "E29.32.5", {"start": v(-49.8, -169.35) * mm, "mid": v(-51.08, -167.3) * mm, "end": v(-53.14, -166.04) * mm});
            skArc(sketch, "E29.32.6", {"start": v(-49.15, -173.27) * mm, "mid": v(-49.33, -171.28) * mm, "end": v(-49.8, -169.35) * mm});
            skLineSegment(sketch, "E29.32.7", {"start": v(-49.15, -173.27) * mm, "end": v(-49.14, -174.36) * mm});
            skLineSegment(sketch, "E29.32.8", {"start": v(-53.6, -165.9) * mm, "end": v(-53.37, -165.97) * mm});
            skLineSegment(sketch, "E29.32.9", {"start": v(-53.14, -166.04) * mm, "end": v(-53.37, -165.97) * mm});
            skArc(sketch, "E29.33.0", {"start": v(-33.54, -178.02) * mm, "mid": v(-33.22, -179.47) * mm, "end": v(-32.58, -180.8) * mm});
            skArc(sketch, "E29.33.1", {"start": v(-46.38, -175.13) * mm, "mid": v(-47.3, -176.3) * mm, "end": v(-48.44, -177.24) * mm});
            skLineSegment(sketch, "E29.33.2", {"start": v(-45.82, -174.2) * mm, "end": v(-46.38, -175.13) * mm});
            skArc(sketch, "E29.33.3", {"start": v(-45.82, -174.2) * mm, "mid": v(-44.66, -172.58) * mm, "end": v(-43.27, -171.15) * mm});
            skArc(sketch, "E29.33.4", {"start": v(-43.27, -171.15) * mm, "mid": v(-41.13, -170.02) * mm, "end": v(-38.72, -169.98) * mm});
            skArc(sketch, "E29.33.5", {"start": v(-34.65, -173.09) * mm, "mid": v(-36.1, -171.15) * mm, "end": v(-38.26, -170.09) * mm});
            skArc(sketch, "E29.33.6", {"start": v(-33.65, -176.94) * mm, "mid": v(-34, -174.97) * mm, "end": v(-34.65, -173.09) * mm});
            skLineSegment(sketch, "E29.33.7", {"start": v(-33.65, -176.94) * mm, "end": v(-33.54, -178.02) * mm});
            skLineSegment(sketch, "E29.33.8", {"start": v(-38.72, -169.98) * mm, "end": v(-38.49, -170.03) * mm});
            skLineSegment(sketch, "E29.33.9", {"start": v(-38.26, -170.09) * mm, "end": v(-38.49, -170.03) * mm});
            skArc(sketch, "E29.34.0", {"start": v(-17.67, -180.28) * mm, "mid": v(-17.23, -181.7) * mm, "end": v(-16.47, -182.98) * mm});
            skArc(sketch, "E29.34.1", {"start": v(-30.72, -178.54) * mm, "mid": v(-31.52, -179.79) * mm, "end": v(-32.58, -180.83) * mm});
            skLineSegment(sketch, "E29.34.2", {"start": v(-30.24, -177.57) * mm, "end": v(-30.72, -178.54) * mm});
            skArc(sketch, "E29.34.3", {"start": v(-30.24, -177.57) * mm, "mid": v(-29.23, -175.85) * mm, "end": v(-27.97, -174.3) * mm});
            skArc(sketch, "E29.34.4", {"start": v(-27.97, -174.3) * mm, "mid": v(-25.95, -172.99) * mm, "end": v(-23.55, -172.74) * mm});
            skArc(sketch, "E29.34.5", {"start": v(-19.21, -175.47) * mm, "mid": v(-20.82, -173.67) * mm, "end": v(-23.07, -172.8) * mm});
            skArc(sketch, "E29.34.6", {"start": v(-17.88, -179.22) * mm, "mid": v(-18.4, -177.3) * mm, "end": v(-19.21, -175.47) * mm});
            skLineSegment(sketch, "E29.34.7", {"start": v(-17.88, -179.22) * mm, "end": v(-17.67, -180.28) * mm});
            skLineSegment(sketch, "E29.34.8", {"start": v(-23.55, -172.74) * mm, "end": v(-23.3, -172.77) * mm});
            skLineSegment(sketch, "E29.34.9", {"start": v(-23.07, -172.8) * mm, "end": v(-23.3, -172.77) * mm});
            skArc(sketch, "E29.35.0", {"start": v(-1.67, -181.14) * mm, "mid": v(-1.1, -182.51) * mm, "end": v(-0.24, -183.72) * mm});
            skArc(sketch, "E29.35.1", {"start": v(-14.82, -180.56) * mm, "mid": v(-15.51, -181.87) * mm, "end": v(-16.48, -183) * mm});
            skLineSegment(sketch, "E29.35.2", {"start": v(-14.43, -179.54) * mm, "end": v(-14.82, -180.56) * mm});
            skArc(sketch, "E29.35.3", {"start": v(-14.43, -179.54) * mm, "mid": v(-13.57, -177.74) * mm, "end": v(-12.46, -176.1) * mm});
            skArc(sketch, "E29.35.4", {"start": v(-12.46, -176.1) * mm, "mid": v(-10.56, -174.6) * mm, "end": v(-8.19, -174.14) * mm});
            skArc(sketch, "E29.35.5", {"start": v(-3.63, -176.48) * mm, "mid": v(-5.4, -174.83) * mm, "end": v(-7.71, -174.17) * mm});
            skArc(sketch, "E29.35.6", {"start": v(-1.97, -180.1) * mm, "mid": v(-2.66, -178.23) * mm, "end": v(-3.63, -176.48) * mm});
            skLineSegment(sketch, "E29.35.7", {"start": v(-1.97, -180.1) * mm, "end": v(-1.67, -181.14) * mm});
            skLineSegment(sketch, "E29.35.8", {"start": v(-8.19, -174.14) * mm, "end": v(-7.95, -174.15) * mm});
            skLineSegment(sketch, "E29.35.9", {"start": v(-7.71, -174.17) * mm, "end": v(-7.95, -174.15) * mm});
            skArc(sketch, "E29.36.0", {"start": v(14.35, -180.58) * mm, "mid": v(15.04, -181.9) * mm, "end": v(16, -183.02) * mm});
            skArc(sketch, "E29.36.1", {"start": v(1.2, -181.16) * mm, "mid": v(0.62, -182.53) * mm, "end": v(-0.24, -183.74) * mm});
            skLineSegment(sketch, "E29.36.2", {"start": v(1.5, -180.12) * mm, "end": v(1.2, -181.16) * mm});
            skArc(sketch, "E29.36.3", {"start": v(1.5, -180.12) * mm, "mid": v(2.19, -178.25) * mm, "end": v(3.16, -176.5) * mm});
            skArc(sketch, "E29.36.4", {"start": v(3.16, -176.5) * mm, "mid": v(4.92, -174.85) * mm, "end": v(7.24, -174.19) * mm});
            skArc(sketch, "E29.36.5", {"start": v(11.98, -176.11) * mm, "mid": v(10.08, -174.63) * mm, "end": v(7.71, -174.17) * mm});
            skArc(sketch, "E29.36.6", {"start": v(13.95, -179.56) * mm, "mid": v(13.1, -177.77) * mm, "end": v(11.98, -176.11) * mm});
            skLineSegment(sketch, "E29.36.7", {"start": v(13.95, -179.56) * mm, "end": v(14.35, -180.58) * mm});
            skLineSegment(sketch, "E29.36.8", {"start": v(7.24, -174.19) * mm, "end": v(7.47, -174.18) * mm});
            skLineSegment(sketch, "E29.36.9", {"start": v(7.71, -174.17) * mm, "end": v(7.47, -174.18) * mm});
            skArc(sketch, "E29.37.0", {"start": v(30.25, -178.6) * mm, "mid": v(31.05, -179.85) * mm, "end": v(32.11, -180.9) * mm});
            skArc(sketch, "E29.37.1", {"start": v(17.2, -180.35) * mm, "mid": v(16.75, -181.76) * mm, "end": v(16, -183.04) * mm});
            skLineSegment(sketch, "E29.37.2", {"start": v(17.4, -179.28) * mm, "end": v(17.2, -180.35) * mm});
            skArc(sketch, "E29.37.3", {"start": v(17.4, -179.28) * mm, "mid": v(17.93, -177.36) * mm, "end": v(18.74, -175.54) * mm});
            skArc(sketch, "E29.37.4", {"start": v(18.74, -175.54) * mm, "mid": v(20.35, -173.74) * mm, "end": v(22.6, -172.87) * mm});
            skArc(sketch, "E29.37.5", {"start": v(27.5, -174.37) * mm, "mid": v(25.47, -173.05) * mm, "end": v(23.07, -172.8) * mm});
            skArc(sketch, "E29.37.6", {"start": v(29.77, -177.63) * mm, "mid": v(28.76, -175.91) * mm, "end": v(27.5, -174.37) * mm});
            skLineSegment(sketch, "E29.37.7", {"start": v(29.77, -177.63) * mm, "end": v(30.25, -178.6) * mm});
            skLineSegment(sketch, "E29.37.8", {"start": v(22.6, -172.87) * mm, "end": v(22.84, -172.83) * mm});
            skLineSegment(sketch, "E29.37.9", {"start": v(23.07, -172.8) * mm, "end": v(22.84, -172.83) * mm});
            skArc(sketch, "E29.38.0", {"start": v(45.92, -175.23) * mm, "mid": v(46.83, -176.4) * mm, "end": v(47.97, -177.34) * mm});
            skArc(sketch, "E29.38.1", {"start": v(33.07, -178.12) * mm, "mid": v(32.75, -179.57) * mm, "end": v(32.12, -180.91) * mm});
            skLineSegment(sketch, "E29.38.2", {"start": v(33.18, -177.04) * mm, "end": v(33.07, -178.12) * mm});
            skArc(sketch, "E29.38.3", {"start": v(33.18, -177.04) * mm, "mid": v(33.54, -175.08) * mm, "end": v(34.18, -173.2) * mm});
            skArc(sketch, "E29.38.4", {"start": v(34.18, -173.2) * mm, "mid": v(35.63, -171.26) * mm, "end": v(37.8, -170.2) * mm});
            skArc(sketch, "E29.38.5", {"start": v(42.8, -171.25) * mm, "mid": v(40.67, -170.12) * mm, "end": v(38.26, -170.09) * mm});
            skArc(sketch, "E29.38.6", {"start": v(45.35, -174.3) * mm, "mid": v(44.2, -172.68) * mm, "end": v(42.8, -171.25) * mm});
            skLineSegment(sketch, "E29.38.7", {"start": v(45.35, -174.3) * mm, "end": v(45.92, -175.23) * mm});
            skLineSegment(sketch, "E29.38.8", {"start": v(37.8, -170.2) * mm, "end": v(38.02, -170.14) * mm});
            skLineSegment(sketch, "E29.38.9", {"start": v(38.26, -170.09) * mm, "end": v(38.02, -170.14) * mm});
            skArc(sketch, "E29.39.0", {"start": v(61.23, -170.49) * mm, "mid": v(62.23, -171.58) * mm, "end": v(63.46, -172.41) * mm});
            skArc(sketch, "E29.39.1", {"start": v(48.68, -174.5) * mm, "mid": v(48.5, -175.97) * mm, "end": v(47.98, -177.36) * mm});
            skLineSegment(sketch, "E29.39.2", {"start": v(48.7, -173.41) * mm, "end": v(48.68, -174.5) * mm});
            skArc(sketch, "E29.39.3", {"start": v(48.7, -173.41) * mm, "mid": v(48.88, -171.43) * mm, "end": v(49.36, -169.5) * mm});
            skArc(sketch, "E29.39.4", {"start": v(49.36, -169.5) * mm, "mid": v(50.62, -167.44) * mm, "end": v(52.69, -166.19) * mm});
            skArc(sketch, "E29.39.5", {"start": v(57.77, -166.8) * mm, "mid": v(55.55, -165.86) * mm, "end": v(53.14, -166.04) * mm});
            skArc(sketch, "E29.39.6", {"start": v(60.58, -169.61) * mm, "mid": v(59.28, -168.1) * mm, "end": v(57.77, -166.8) * mm});
            skLineSegment(sketch, "E29.39.7", {"start": v(60.58, -169.61) * mm, "end": v(61.23, -170.49) * mm});
            skLineSegment(sketch, "E29.39.8", {"start": v(52.69, -166.19) * mm, "end": v(52.91, -166.11) * mm});
            skLineSegment(sketch, "E29.39.9", {"start": v(53.14, -166.04) * mm, "end": v(52.91, -166.11) * mm});
            skArc(sketch, "E29.40.0", {"start": v(76.05, -164.41) * mm, "mid": v(77.15, -165.4) * mm, "end": v(78.45, -166.13) * mm});
            skArc(sketch, "E29.40.1", {"start": v(63.92, -169.52) * mm, "mid": v(63.86, -171) * mm, "end": v(63.47, -172.43) * mm});
            skLineSegment(sketch, "E29.40.2", {"start": v(63.84, -168.43) * mm, "end": v(63.92, -169.52) * mm});
            skArc(sketch, "E29.40.3", {"start": v(63.84, -168.43) * mm, "mid": v(63.84, -166.44) * mm, "end": v(64.14, -164.47) * mm});
            skArc(sketch, "E29.40.4", {"start": v(64.14, -164.47) * mm, "mid": v(65.22, -162.3) * mm, "end": v(67.17, -160.88) * mm});
            skArc(sketch, "E29.40.5", {"start": v(72.29, -161.04) * mm, "mid": v(69.99, -160.3) * mm, "end": v(67.6, -160.7) * mm});
            skArc(sketch, "E29.40.6", {"start": v(75.33, -163.6) * mm, "mid": v(73.9, -162.2) * mm, "end": v(72.29, -161.04) * mm});
            skLineSegment(sketch, "E29.40.7", {"start": v(75.33, -163.6) * mm, "end": v(76.05, -164.41) * mm});
            skLineSegment(sketch, "E29.40.8", {"start": v(67.17, -160.88) * mm, "end": v(67.39, -160.79) * mm});
            skLineSegment(sketch, "E29.40.9", {"start": v(67.6, -160.7) * mm, "end": v(67.39, -160.79) * mm});
            skArc(sketch, "E29.41.0", {"start": v(90.29, -157.05) * mm, "mid": v(91.47, -157.94) * mm, "end": v(92.82, -158.54) * mm});
            skArc(sketch, "E29.41.1", {"start": v(78.65, -163.2) * mm, "mid": v(78.72, -164.69) * mm, "end": v(78.46, -166.15) * mm});
            skLineSegment(sketch, "E29.41.2", {"start": v(78.47, -162.13) * mm, "end": v(78.65, -163.2) * mm});
            skArc(sketch, "E29.41.3", {"start": v(78.47, -162.13) * mm, "mid": v(78.3, -160.14) * mm, "end": v(78.43, -158.16) * mm});
            skArc(sketch, "E29.41.4", {"start": v(78.43, -158.16) * mm, "mid": v(79.31, -155.9) * mm, "end": v(81.12, -154.31) * mm});
            skArc(sketch, "E29.41.5", {"start": v(86.24, -154.02) * mm, "mid": v(83.88, -153.5) * mm, "end": v(81.54, -154.1) * mm});
            skArc(sketch, "E29.41.6", {"start": v(89.5, -156.3) * mm, "mid": v(87.95, -155.04) * mm, "end": v(86.24, -154.02) * mm});
            skLineSegment(sketch, "E29.41.7", {"start": v(89.5, -156.3) * mm, "end": v(90.29, -157.05) * mm});
            skLineSegment(sketch, "E29.41.8", {"start": v(81.12, -154.31) * mm, "end": v(81.33, -154.2) * mm});
            skLineSegment(sketch, "E29.41.9", {"start": v(81.54, -154.1) * mm, "end": v(81.33, -154.2) * mm});
            skArc(sketch, "E29.42.0", {"start": v(103.81, -148.45) * mm, "mid": v(105.07, -149.24) * mm, "end": v(106.47, -149.72) * mm});
            skArc(sketch, "E29.42.1", {"start": v(92.76, -155.61) * mm, "mid": v(92.97, -157.08) * mm, "end": v(92.84, -158.56) * mm});
            skLineSegment(sketch, "E29.42.2", {"start": v(92.5, -154.56) * mm, "end": v(92.76, -155.61) * mm});
            skArc(sketch, "E29.42.3", {"start": v(92.5, -154.56) * mm, "mid": v(92.15, -152.6) * mm, "end": v(92.1, -150.6) * mm});
            skArc(sketch, "E29.42.4", {"start": v(92.1, -150.6) * mm, "mid": v(92.78, -148.29) * mm, "end": v(94.44, -146.54) * mm});
            skArc(sketch, "E29.42.5", {"start": v(99.51, -145.8) * mm, "mid": v(97.12, -145.48) * mm, "end": v(94.84, -146.28) * mm});
            skArc(sketch, "E29.42.6", {"start": v(102.96, -147.78) * mm, "mid": v(101.3, -146.66) * mm, "end": v(99.51, -145.8) * mm});
            skLineSegment(sketch, "E29.42.7", {"start": v(102.96, -147.78) * mm, "end": v(103.81, -148.45) * mm});
            skLineSegment(sketch, "E29.42.8", {"start": v(94.44, -146.54) * mm, "end": v(94.64, -146.4) * mm});
            skLineSegment(sketch, "E29.42.9", {"start": v(94.84, -146.28) * mm, "end": v(94.64, -146.4) * mm});
            skArc(sketch, "E29.43.0", {"start": v(116.53, -138.7) * mm, "mid": v(117.85, -139.37) * mm, "end": v(119.29, -139.72) * mm});
            skArc(sketch, "E29.43.1", {"start": v(106.15, -146.8) * mm, "mid": v(106.49, -148.25) * mm, "end": v(106.49, -149.74) * mm});
            skLineSegment(sketch, "E29.43.2", {"start": v(105.8, -145.78) * mm, "end": v(106.15, -146.8) * mm});
            skArc(sketch, "E29.43.3", {"start": v(105.8, -145.78) * mm, "mid": v(105.27, -143.86) * mm, "end": v(105.05, -141.88) * mm});
            skArc(sketch, "E29.43.4", {"start": v(105.05, -141.88) * mm, "mid": v(105.52, -139.5) * mm, "end": v(107.02, -137.62) * mm});
            skArc(sketch, "E29.43.5", {"start": v(112, -136.43) * mm, "mid": v(109.6, -136.33) * mm, "end": v(107.4, -137.33) * mm});
            skArc(sketch, "E29.43.6", {"start": v(115.62, -138.1) * mm, "mid": v(113.87, -137.13) * mm, "end": v(112, -136.43) * mm});
            skLineSegment(sketch, "E29.43.7", {"start": v(115.62, -138.1) * mm, "end": v(116.53, -138.7) * mm});
            skLineSegment(sketch, "E29.43.8", {"start": v(107.02, -137.62) * mm, "end": v(107.21, -137.47) * mm});
            skLineSegment(sketch, "E29.43.9", {"start": v(107.4, -137.33) * mm, "end": v(107.21, -137.47) * mm});
            skArc(sketch, "E29.44.0", {"start": v(128.33, -127.85) * mm, "mid": v(129.7, -128.4) * mm, "end": v(131.17, -128.63) * mm});
            skArc(sketch, "E29.44.1", {"start": v(118.71, -136.85) * mm, "mid": v(119.17, -138.26) * mm, "end": v(119.3, -139.74) * mm});
            skLineSegment(sketch, "E29.44.2", {"start": v(118.26, -135.86) * mm, "end": v(118.71, -136.85) * mm});
            skArc(sketch, "E29.44.3", {"start": v(118.26, -135.86) * mm, "mid": v(117.58, -133.99) * mm, "end": v(117.18, -132.04) * mm});
            skArc(sketch, "E29.44.4", {"start": v(117.18, -132.04) * mm, "mid": v(117.44, -129.64) * mm, "end": v(118.77, -127.62) * mm});
            skArc(sketch, "E29.44.5", {"start": v(123.63, -126) * mm, "mid": v(121.22, -126.1) * mm, "end": v(119.12, -127.3) * mm});
            skArc(sketch, "E29.44.6", {"start": v(127.37, -127.34) * mm, "mid": v(125.55, -126.53) * mm, "end": v(123.63, -126) * mm});
            skLineSegment(sketch, "E29.44.7", {"start": v(127.37, -127.34) * mm, "end": v(128.33, -127.85) * mm});
            skLineSegment(sketch, "E29.44.8", {"start": v(118.77, -127.62) * mm, "end": v(118.94, -127.46) * mm});
            skLineSegment(sketch, "E29.44.9", {"start": v(119.12, -127.3) * mm, "end": v(118.94, -127.46) * mm});
            skArc(sketch, "E29.45.0", {"start": v(139.13, -116.01) * mm, "mid": v(140.55, -116.44) * mm, "end": v(142.03, -116.54) * mm});
            skArc(sketch, "E29.45.1", {"start": v(130.34, -125.82) * mm, "mid": v(130.93, -127.19) * mm, "end": v(131.19, -128.65) * mm});
            skLineSegment(sketch, "E29.45.2", {"start": v(129.8, -124.88) * mm, "end": v(130.34, -125.82) * mm});
            skArc(sketch, "E29.45.3", {"start": v(129.8, -124.88) * mm, "mid": v(128.96, -123.07) * mm, "end": v(128.39, -121.16) * mm});
            skArc(sketch, "E29.45.4", {"start": v(128.39, -121.16) * mm, "mid": v(128.44, -118.75) * mm, "end": v(129.58, -116.63) * mm});
            skArc(sketch, "E29.45.5", {"start": v(134.28, -114.58) * mm, "mid": v(131.89, -114.9) * mm, "end": v(129.9, -116.27) * mm});
            skArc(sketch, "E29.45.6", {"start": v(138.13, -115.58) * mm, "mid": v(136.24, -114.94) * mm, "end": v(134.28, -114.58) * mm});
            skLineSegment(sketch, "E29.45.7", {"start": v(138.13, -115.58) * mm, "end": v(139.13, -116.01) * mm});
            skLineSegment(sketch, "E29.45.8", {"start": v(129.58, -116.63) * mm, "end": v(129.74, -116.45) * mm});
            skLineSegment(sketch, "E29.45.9", {"start": v(129.9, -116.27) * mm, "end": v(129.74, -116.45) * mm});
            skArc(sketch, "E29.46.0", {"start": v(148.83, -103.26) * mm, "mid": v(150.29, -103.56) * mm, "end": v(151.77, -103.53) * mm});
            skArc(sketch, "E29.46.1", {"start": v(140.95, -113.81) * mm, "mid": v(141.65, -115.12) * mm, "end": v(142.04, -116.55) * mm});
            skLineSegment(sketch, "E29.46.2", {"start": v(140.34, -112.92) * mm, "end": v(140.95, -113.81) * mm});
            skArc(sketch, "E29.46.3", {"start": v(140.34, -112.92) * mm, "mid": v(139.33, -111.2) * mm, "end": v(138.6, -109.34) * mm});
            skArc(sketch, "E29.46.4", {"start": v(138.6, -109.34) * mm, "mid": v(138.43, -106.93) * mm, "end": v(139.38, -104.72) * mm});
            skArc(sketch, "E29.46.5", {"start": v(143.88, -102.27) * mm, "mid": v(141.53, -102.8) * mm, "end": v(139.67, -104.34) * mm});
            skArc(sketch, "E29.46.6", {"start": v(147.8, -102.92) * mm, "mid": v(145.87, -102.45) * mm, "end": v(143.88, -102.27) * mm});
            skLineSegment(sketch, "E29.46.7", {"start": v(147.8, -102.92) * mm, "end": v(148.83, -103.26) * mm});
            skLineSegment(sketch, "E29.46.8", {"start": v(139.38, -104.72) * mm, "end": v(139.53, -104.53) * mm});
            skLineSegment(sketch, "E29.46.9", {"start": v(139.67, -104.34) * mm, "end": v(139.53, -104.53) * mm});
            skArc(sketch, "E29.47.0", {"start": v(157.38, -89.7) * mm, "mid": v(158.85, -89.87) * mm, "end": v(160.33, -89.71) * mm});
            skArc(sketch, "E29.47.1", {"start": v(150.46, -100.9) * mm, "mid": v(151.27, -102.15) * mm, "end": v(151.79, -103.54) * mm});
            skLineSegment(sketch, "E29.47.2", {"start": v(149.77, -100.07) * mm, "end": v(150.46, -100.9) * mm});
            skArc(sketch, "E29.47.3", {"start": v(149.77, -100.07) * mm, "mid": v(148.61, -98.45) * mm, "end": v(147.72, -96.67) * mm});
            skArc(sketch, "E29.47.4", {"start": v(147.72, -96.67) * mm, "mid": v(147.34, -94.28) * mm, "end": v(148.1, -91.99) * mm});
            skArc(sketch, "E29.47.5", {"start": v(152.36, -89.15) * mm, "mid": v(150.06, -89.88) * mm, "end": v(148.34, -91.58) * mm});
            skArc(sketch, "E29.47.6", {"start": v(156.32, -89.46) * mm, "mid": v(154.35, -89.15) * mm, "end": v(152.36, -89.15) * mm});
            skLineSegment(sketch, "E29.47.7", {"start": v(156.32, -89.46) * mm, "end": v(157.38, -89.7) * mm});
            skLineSegment(sketch, "E29.47.8", {"start": v(148.1, -91.99) * mm, "end": v(148.22, -91.79) * mm});
            skLineSegment(sketch, "E29.47.9", {"start": v(148.34, -91.58) * mm, "end": v(148.22, -91.79) * mm});
            skArc(sketch, "E29.48.0", {"start": v(164.7, -75.44) * mm, "mid": v(166.17, -75.48) * mm, "end": v(167.63, -75.19) * mm});
            skArc(sketch, "E29.48.1", {"start": v(158.8, -87.22) * mm, "mid": v(159.7, -88.38) * mm, "end": v(160.34, -89.72) * mm});
            skLineSegment(sketch, "E29.48.2", {"start": v(158.02, -86.44) * mm, "end": v(158.8, -87.22) * mm});
            skArc(sketch, "E29.48.3", {"start": v(158.02, -86.44) * mm, "mid": v(156.73, -84.93) * mm, "end": v(155.68, -83.23) * mm});
            skArc(sketch, "E29.48.4", {"start": v(155.68, -83.23) * mm, "mid": v(155.1, -80.9) * mm, "end": v(155.64, -78.54) * mm});
            skArc(sketch, "E29.48.5", {"start": v(159.64, -75.34) * mm, "mid": v(157.41, -76.27) * mm, "end": v(155.86, -78.11) * mm});
            skArc(sketch, "E29.48.6", {"start": v(163.61, -75.3) * mm, "mid": v(161.62, -75.16) * mm, "end": v(159.64, -75.34) * mm});
            skLineSegment(sketch, "E29.48.7", {"start": v(163.61, -75.3) * mm, "end": v(164.7, -75.44) * mm});
            skLineSegment(sketch, "E29.48.8", {"start": v(155.64, -78.54) * mm, "end": v(155.75, -78.33) * mm});
            skLineSegment(sketch, "E29.48.9", {"start": v(155.86, -78.11) * mm, "end": v(155.75, -78.33) * mm});
            skArc(sketch, "E29.49.0", {"start": v(170.71, -60.6) * mm, "mid": v(172.2, -60.5) * mm, "end": v(173.62, -60.08) * mm});
            skArc(sketch, "E29.49.1", {"start": v(165.88, -72.84) * mm, "mid": v(166.9, -73.92) * mm, "end": v(167.65, -75.2) * mm});
            skLineSegment(sketch, "E29.49.2", {"start": v(165.05, -72.14) * mm, "end": v(165.88, -72.84) * mm});
            skArc(sketch, "E29.49.3", {"start": v(165.05, -72.14) * mm, "mid": v(163.62, -70.74) * mm, "end": v(162.43, -69.15) * mm});
            skArc(sketch, "E29.49.4", {"start": v(162.43, -69.15) * mm, "mid": v(161.64, -66.87) * mm, "end": v(161.98, -64.48) * mm});
            skArc(sketch, "E29.49.5", {"start": v(165.67, -60.93) * mm, "mid": v(163.54, -62.06) * mm, "end": v(162.15, -64.03) * mm});
            skArc(sketch, "E29.49.6", {"start": v(169.63, -60.54) * mm, "mid": v(167.63, -60.59) * mm, "end": v(165.67, -60.93) * mm});
            skLineSegment(sketch, "E29.49.7", {"start": v(169.63, -60.54) * mm, "end": v(170.71, -60.6) * mm});
            skLineSegment(sketch, "E29.49.8", {"start": v(161.98, -64.48) * mm, "end": v(162.06, -64.26) * mm});
            skLineSegment(sketch, "E29.49.9", {"start": v(162.15, -64.03) * mm, "end": v(162.06, -64.26) * mm});
            skArc(sketch, "E29.50.0", {"start": v(175.4, -45.27) * mm, "mid": v(176.87, -45.05) * mm, "end": v(178.25, -44.5) * mm});
            skArc(sketch, "E29.50.1", {"start": v(171.67, -57.9) * mm, "mid": v(172.78, -58.88) * mm, "end": v(173.64, -60.09) * mm});
            skLineSegment(sketch, "E29.50.2", {"start": v(170.78, -57.27) * mm, "end": v(171.67, -57.9) * mm});
            skArc(sketch, "E29.50.3", {"start": v(170.78, -57.27) * mm, "mid": v(169.24, -56) * mm, "end": v(167.9, -54.52) * mm});
            skArc(sketch, "E29.50.4", {"start": v(167.9, -54.52) * mm, "mid": v(166.92, -52.32) * mm, "end": v(167.04, -49.9) * mm});
            skArc(sketch, "E29.50.5", {"start": v(170.4, -46.05) * mm, "mid": v(168.38, -47.36) * mm, "end": v(167.17, -49.45) * mm});
            skArc(sketch, "E29.50.6", {"start": v(174.31, -45.3) * mm, "mid": v(172.33, -45.53) * mm, "end": v(170.4, -46.05) * mm});
            skLineSegment(sketch, "E29.50.7", {"start": v(174.31, -45.3) * mm, "end": v(175.4, -45.27) * mm});
            skLineSegment(sketch, "E29.50.8", {"start": v(167.04, -49.9) * mm, "end": v(167.1, -49.68) * mm});
            skLineSegment(sketch, "E29.50.9", {"start": v(167.17, -49.45) * mm, "end": v(167.1, -49.68) * mm});
            skArc(sketch, "E29.51.0", {"start": v(178.72, -29.59) * mm, "mid": v(180.16, -29.24) * mm, "end": v(181.48, -28.57) * mm});
            skArc(sketch, "E29.51.1", {"start": v(176.11, -42.5) * mm, "mid": v(177.3, -43.38) * mm, "end": v(178.27, -44.5) * mm});
            skLineSegment(sketch, "E29.51.2", {"start": v(175.17, -41.95) * mm, "end": v(176.11, -42.5) * mm});
            skArc(sketch, "E29.51.3", {"start": v(175.17, -41.95) * mm, "mid": v(173.52, -40.83) * mm, "end": v(172.06, -39.47) * mm});
            skArc(sketch, "E29.51.4", {"start": v(172.06, -39.47) * mm, "mid": v(170.89, -37.36) * mm, "end": v(170.8, -34.95) * mm});
            skArc(sketch, "E29.51.5", {"start": v(173.81, -30.81) * mm, "mid": v(171.9, -32.3) * mm, "end": v(170.9, -34.48) * mm});
            skArc(sketch, "E29.51.6", {"start": v(177.64, -29.73) * mm, "mid": v(175.68, -30.12) * mm, "end": v(173.81, -30.81) * mm});
            skLineSegment(sketch, "E29.51.7", {"start": v(177.64, -29.73) * mm, "end": v(178.72, -29.59) * mm});
            skLineSegment(sketch, "E29.51.8", {"start": v(170.8, -34.95) * mm, "end": v(170.84, -34.72) * mm});
            skLineSegment(sketch, "E29.51.9", {"start": v(170.9, -34.48) * mm, "end": v(170.84, -34.72) * mm});
            skArc(sketch, "E29.52.0", {"start": v(180.63, -13.68) * mm, "mid": v(182.04, -13.2) * mm, "end": v(183.3, -12.42) * mm});
            skArc(sketch, "E29.52.1", {"start": v(179.18, -26.77) * mm, "mid": v(180.44, -27.54) * mm, "end": v(181.5, -28.58) * mm});
            skLineSegment(sketch, "E29.52.2", {"start": v(178.2, -26.3) * mm, "end": v(179.18, -26.77) * mm});
            skArc(sketch, "E29.52.3", {"start": v(178.2, -26.3) * mm, "mid": v(176.45, -25.33) * mm, "end": v(174.88, -24.1) * mm});
            skArc(sketch, "E29.52.4", {"start": v(174.88, -24.1) * mm, "mid": v(173.52, -22.11) * mm, "end": v(173.22, -19.72) * mm});
            skArc(sketch, "E29.52.5", {"start": v(175.85, -15.33) * mm, "mid": v(174.1, -16.98) * mm, "end": v(173.27, -19.25) * mm});
            skArc(sketch, "E29.52.6", {"start": v(179.57, -13.91) * mm, "mid": v(177.66, -14.48) * mm, "end": v(175.85, -15.33) * mm});
            skLineSegment(sketch, "E29.52.7", {"start": v(179.57, -13.91) * mm, "end": v(180.63, -13.68) * mm});
            skLineSegment(sketch, "E29.52.8", {"start": v(173.22, -19.72) * mm, "end": v(173.24, -19.48) * mm});
            skLineSegment(sketch, "E29.52.9", {"start": v(173.27, -19.25) * mm, "end": v(173.24, -19.48) * mm});
            skArc(sketch, "E29.53.0", {"start": v(181.13, 2.34) * mm, "mid": v(182.5, 2.94) * mm, "end": v(183.68, 3.83) * mm});
            skArc(sketch, "E29.53.1", {"start": v(180.84, -10.83) * mm, "mid": v(182.17, -11.48) * mm, "end": v(183.32, -12.42) * mm});
            skLineSegment(sketch, "E29.53.2", {"start": v(179.82, -10.45) * mm, "end": v(180.84, -10.83) * mm});
            skArc(sketch, "E29.53.3", {"start": v(179.82, -10.45) * mm, "mid": v(178, -9.64) * mm, "end": v(176.33, -8.56) * mm});
            skArc(sketch, "E29.53.4", {"start": v(176.33, -8.56) * mm, "mid": v(174.8, -6.7) * mm, "end": v(174.28, -4.33) * mm});
            skArc(sketch, "E29.53.5", {"start": v(176.52, 0.27) * mm, "mid": v(174.9, -1.52) * mm, "end": v(174.3, -3.86) * mm});
            skArc(sketch, "E29.53.6", {"start": v(180.1, 2.01) * mm, "mid": v(178.24, 1.28) * mm, "end": v(176.52, 0.27) * mm});
            skLineSegment(sketch, "E29.53.7", {"start": v(180.1, 2.01) * mm, "end": v(181.13, 2.34) * mm});
            skLineSegment(sketch, "E29.53.8", {"start": v(174.28, -4.33) * mm, "end": v(174.29, -4.1) * mm});
            skLineSegment(sketch, "E29.53.9", {"start": v(174.3, -3.86) * mm, "end": v(174.29, -4.1) * mm});
            skArc(sketch, "E29.54.0", {"start": v(180.22, 18.34) * mm, "mid": v(181.52, 19.06) * mm, "end": v(182.62, 20.05) * mm});
            skArc(sketch, "E29.54.1", {"start": v(181.1, 5.2) * mm, "mid": v(182.47, 4.66) * mm, "end": v(183.7, 3.83) * mm});
            skLineSegment(sketch, "E29.54.2", {"start": v(180.04, 5.48) * mm, "end": v(181.1, 5.2) * mm});
            skArc(sketch, "E29.54.3", {"start": v(180.04, 5.48) * mm, "mid": v(178.16, 6.13) * mm, "end": v(176.4, 7.06) * mm});
            skArc(sketch, "E29.54.4", {"start": v(176.4, 7.06) * mm, "mid": v(174.7, 8.78) * mm, "end": v(173.98, 11.09) * mm});
            skArc(sketch, "E29.54.5", {"start": v(175.8, 15.87) * mm, "mid": v(174.36, 13.94) * mm, "end": v(173.95, 11.56) * mm});
            skArc(sketch, "E29.54.6", {"start": v(179.21, 17.92) * mm, "mid": v(177.43, 17.03) * mm, "end": v(175.8, 15.87) * mm});
            skLineSegment(sketch, "E29.54.7", {"start": v(179.21, 17.92) * mm, "end": v(180.22, 18.34) * mm});
            skLineSegment(sketch, "E29.54.8", {"start": v(173.98, 11.09) * mm, "end": v(173.97, 11.32) * mm});
            skLineSegment(sketch, "E29.54.9", {"start": v(173.95, 11.56) * mm, "end": v(173.97, 11.32) * mm});
            skArc(sketch, "E29.55.0", {"start": v(177.9, 34.2) * mm, "mid": v(179.12, 35.02) * mm, "end": v(180.14, 36.1) * mm});
            skArc(sketch, "E29.55.1", {"start": v(179.92, 21.18) * mm, "mid": v(181.35, 20.77) * mm, "end": v(182.64, 20.05) * mm});
            skLineSegment(sketch, "E29.55.2", {"start": v(178.85, 21.37) * mm, "end": v(179.92, 21.18) * mm});
            skArc(sketch, "E29.55.3", {"start": v(178.85, 21.37) * mm, "mid": v(176.92, 21.85) * mm, "end": v(175.08, 22.62) * mm});
            skArc(sketch, "E29.55.4", {"start": v(175.08, 22.62) * mm, "mid": v(173.24, 24.19) * mm, "end": v(172.32, 26.42) * mm});
            skArc(sketch, "E29.55.5", {"start": v(173.72, 31.35) * mm, "mid": v(172.45, 29.3) * mm, "end": v(172.25, 26.9) * mm});
            skArc(sketch, "E29.55.6", {"start": v(176.93, 33.7) * mm, "mid": v(175.23, 32.64) * mm, "end": v(173.72, 31.35) * mm});
            skLineSegment(sketch, "E29.55.7", {"start": v(176.93, 33.7) * mm, "end": v(177.9, 34.2) * mm});
            skLineSegment(sketch, "E29.55.8", {"start": v(172.32, 26.42) * mm, "end": v(172.29, 26.66) * mm});
            skLineSegment(sketch, "E29.55.9", {"start": v(172.25, 26.9) * mm, "end": v(172.29, 26.66) * mm});
            skArc(sketch, "E29.56.0", {"start": v(174.17, 49.78) * mm, "mid": v(175.33, 50.72) * mm, "end": v(176.24, 51.89) * mm});
            skArc(sketch, "E29.56.1", {"start": v(177.35, 37) * mm, "mid": v(178.8, 36.72) * mm, "end": v(180.16, 36.11) * mm});
            skLineSegment(sketch, "E29.56.2", {"start": v(176.26, 37.1) * mm, "end": v(177.35, 37) * mm});
            skArc(sketch, "E29.56.3", {"start": v(176.26, 37.1) * mm, "mid": v(174.3, 37.4) * mm, "end": v(172.4, 38) * mm});
            skArc(sketch, "E29.56.4", {"start": v(172.4, 38) * mm, "mid": v(170.43, 39.4) * mm, "end": v(169.31, 41.55) * mm});
            skArc(sketch, "E29.56.5", {"start": v(170.27, 46.58) * mm, "mid": v(169.18, 44.42) * mm, "end": v(169.2, 42) * mm});
            skArc(sketch, "E29.56.6", {"start": v(173.26, 49.2) * mm, "mid": v(171.66, 48) * mm, "end": v(170.27, 46.58) * mm});
            skLineSegment(sketch, "E29.56.7", {"start": v(173.26, 49.2) * mm, "end": v(174.17, 49.78) * mm});
            skLineSegment(sketch, "E29.56.8", {"start": v(169.31, 41.55) * mm, "end": v(169.26, 41.78) * mm});
            skLineSegment(sketch, "E29.56.9", {"start": v(169.2, 42) * mm, "end": v(169.26, 41.78) * mm});
            skArc(sketch, "E29.57.0", {"start": v(169.1, 64.98) * mm, "mid": v(170.16, 66.01) * mm, "end": v(170.96, 67.26) * mm});
            skArc(sketch, "E29.57.1", {"start": v(173.38, 52.53) * mm, "mid": v(174.86, 52.38) * mm, "end": v(176.26, 51.9) * mm});
            skLineSegment(sketch, "E29.57.2", {"start": v(172.3, 52.53) * mm, "end": v(173.38, 52.53) * mm});
            skArc(sketch, "E29.57.3", {"start": v(172.3, 52.53) * mm, "mid": v(170.3, 52.66) * mm, "end": v(168.36, 53.1) * mm});
            skArc(sketch, "E29.57.4", {"start": v(168.36, 53.1) * mm, "mid": v(166.28, 54.31) * mm, "end": v(164.98, 56.35) * mm});
            skArc(sketch, "E29.57.5", {"start": v(165.48, 61.45) * mm, "mid": v(164.6, 59.2) * mm, "end": v(164.82, 56.8) * mm});
            skArc(sketch, "E29.57.6", {"start": v(168.23, 64.32) * mm, "mid": v(166.75, 62.98) * mm, "end": v(165.48, 61.45) * mm});
            skLineSegment(sketch, "E29.57.7", {"start": v(168.23, 64.32) * mm, "end": v(169.1, 64.98) * mm});
            skLineSegment(sketch, "E29.57.8", {"start": v(164.98, 56.35) * mm, "end": v(164.9, 56.57) * mm});
            skLineSegment(sketch, "E29.57.9", {"start": v(164.82, 56.8) * mm, "end": v(164.9, 56.57) * mm});
            skArc(sketch, "E29.58.0", {"start": v(162.69, 79.67) * mm, "mid": v(163.66, 80.8) * mm, "end": v(164.35, 82.1) * mm});
            skArc(sketch, "E29.58.1", {"start": v(168.06, 67.65) * mm, "mid": v(169.54, 67.62) * mm, "end": v(170.98, 67.27) * mm});
            skLineSegment(sketch, "E29.58.2", {"start": v(166.98, 67.55) * mm, "end": v(168.06, 67.65) * mm});
            skArc(sketch, "E29.58.3", {"start": v(166.98, 67.55) * mm, "mid": v(164.99, 67.5) * mm, "end": v(163, 67.77) * mm});
            skArc(sketch, "E29.58.4", {"start": v(163, 67.77) * mm, "mid": v(160.83, 68.8) * mm, "end": v(159.35, 70.7) * mm});
            skArc(sketch, "E29.58.5", {"start": v(159.4, 75.83) * mm, "mid": v(158.72, 73.52) * mm, "end": v(159.16, 71.14) * mm});
            skArc(sketch, "E29.58.6", {"start": v(161.89, 78.93) * mm, "mid": v(160.53, 77.48) * mm, "end": v(159.4, 75.83) * mm});
            skLineSegment(sketch, "E29.58.7", {"start": v(161.89, 78.93) * mm, "end": v(162.69, 79.67) * mm});
            skLineSegment(sketch, "E29.58.8", {"start": v(159.35, 70.7) * mm, "end": v(159.26, 70.93) * mm});
            skLineSegment(sketch, "E29.58.9", {"start": v(159.16, 71.14) * mm, "end": v(159.26, 70.93) * mm});
            skArc(sketch, "E29.59.0", {"start": v(155, 93.74) * mm, "mid": v(155.88, 94.94) * mm, "end": v(156.45, 96.3) * mm});
            skArc(sketch, "E29.59.1", {"start": v(161.42, 82.24) * mm, "mid": v(162.9, 82.34) * mm, "end": v(164.37, 82.11) * mm});
            skLineSegment(sketch, "E29.59.2", {"start": v(160.35, 82.04) * mm, "end": v(161.42, 82.24) * mm});
            skArc(sketch, "E29.59.3", {"start": v(160.35, 82.04) * mm, "mid": v(158.37, 81.82) * mm, "end": v(156.38, 81.9) * mm});
            skArc(sketch, "E29.59.4", {"start": v(156.38, 81.9) * mm, "mid": v(154.12, 82.74) * mm, "end": v(152.48, 84.52) * mm});
            skArc(sketch, "E29.59.5", {"start": v(152.08, 89.62) * mm, "mid": v(151.6, 87.26) * mm, "end": v(152.25, 84.93) * mm});
            skArc(sketch, "E29.59.6", {"start": v(154.28, 92.93) * mm, "mid": v(153.05, 91.36) * mm, "end": v(152.08, 89.62) * mm});
            skLineSegment(sketch, "E29.59.7", {"start": v(154.28, 92.93) * mm, "end": v(155, 93.74) * mm});
            skLineSegment(sketch, "E29.59.8", {"start": v(152.48, 84.52) * mm, "end": v(152.36, 84.72) * mm});
            skLineSegment(sketch, "E29.59.9", {"start": v(152.25, 84.93) * mm, "end": v(152.36, 84.72) * mm});
            skArc(sketch, "E29.60.0", {"start": v(146.12, 107.07) * mm, "mid": v(146.88, 108.35) * mm, "end": v(147.33, 109.76) * mm});
            skArc(sketch, "E29.60.1", {"start": v(153.52, 96.18) * mm, "mid": v(154.99, 96.42) * mm, "end": v(156.47, 96.32) * mm});
            skLineSegment(sketch, "E29.60.2", {"start": v(152.48, 95.9) * mm, "end": v(153.52, 96.18) * mm});
            skArc(sketch, "E29.60.3", {"start": v(152.48, 95.9) * mm, "mid": v(150.52, 95.5) * mm, "end": v(148.53, 95.4) * mm});
            skArc(sketch, "E29.60.4", {"start": v(148.53, 95.4) * mm, "mid": v(146.2, 96.04) * mm, "end": v(144.41, 97.66) * mm});
            skArc(sketch, "E29.60.5", {"start": v(143.56, 102.71) * mm, "mid": v(143.3, 100.31) * mm, "end": v(144.15, 98.06) * mm});
            skArc(sketch, "E29.60.6", {"start": v(145.46, 106.2) * mm, "mid": v(144.38, 104.53) * mm, "end": v(143.56, 102.71) * mm});
            skLineSegment(sketch, "E29.60.7", {"start": v(145.46, 106.2) * mm, "end": v(146.12, 107.07) * mm});
            skLineSegment(sketch, "E29.60.8", {"start": v(144.41, 97.66) * mm, "end": v(144.28, 97.86) * mm});
            skLineSegment(sketch, "E29.60.9", {"start": v(144.15, 98.06) * mm, "end": v(144.28, 97.86) * mm});
            skPoint(sketch, "E29.center", {"position": v(0, 0) * mm});
            skArc(sketch, "E30.1.61.0", {"start": v(136.08, 119.57) * mm, "mid": v(136.72, 120.9) * mm, "end": v(137.05, 122.35) * mm});
            skArc(sketch, "E30.4.61.0", {"start": v(144.42, 109.38) * mm, "mid": v(145.86, 109.74) * mm, "end": v(147.34, 109.77) * mm});
            skLineSegment(sketch, "E30.8.61.0", {"start": v(143.4, 109) * mm, "end": v(144.42, 109.38) * mm});
            skArc(sketch, "E30.11.61.0", {"start": v(143.4, 109) * mm, "mid": v(141.5, 108.43) * mm, "end": v(139.52, 108.16) * mm});
            skArc(sketch, "E30.15.61.0", {"start": v(139.52, 108.16) * mm, "mid": v(137.14, 108.58) * mm, "end": v(135.22, 110.04) * mm});
            skArc(sketch, "E30.19.61.0", {"start": v(133.92, 115) * mm, "mid": v(133.87, 112.58) * mm, "end": v(134.92, 110.41) * mm});
            skArc(sketch, "E30.23.61.0", {"start": v(135.5, 118.64) * mm, "mid": v(134.58, 116.88) * mm, "end": v(133.92, 115) * mm});
            skLineSegment(sketch, "E30.27.61.0", {"start": v(135.5, 118.64) * mm, "end": v(136.08, 119.57) * mm});
            skLineSegment(sketch, "E30.30.61.0", {"start": v(135.22, 110.04) * mm, "end": v(135.07, 110.23) * mm});
            skLineSegment(sketch, "E30.33.61.0", {"start": v(134.92, 110.41) * mm, "end": v(135.07, 110.23) * mm});
            skArc(sketch, "E30.1.62.0", {"start": v(124.98, 131.13) * mm, "mid": v(125.5, 132.51) * mm, "end": v(125.7, 133.98) * mm});
            skArc(sketch, "E30.4.62.0", {"start": v(134.2, 121.71) * mm, "mid": v(135.6, 122.2) * mm, "end": v(137.07, 122.37) * mm});
            skLineSegment(sketch, "E30.8.62.0", {"start": v(133.21, 121.24) * mm, "end": v(134.2, 121.71) * mm});
            skArc(sketch, "E30.11.62.0", {"start": v(133.21, 121.24) * mm, "mid": v(131.36, 120.51) * mm, "end": v(129.41, 120.07) * mm});
            skArc(sketch, "E30.15.62.0", {"start": v(129.41, 120.07) * mm, "mid": v(127, 120.28) * mm, "end": v(124.96, 121.56) * mm});
            skArc(sketch, "E30.19.62.0", {"start": v(123.24, 126.38) * mm, "mid": v(123.4, 123.98) * mm, "end": v(124.63, 121.9) * mm});
            skArc(sketch, "E30.23.62.0", {"start": v(124.49, 130.16) * mm, "mid": v(123.72, 128.32) * mm, "end": v(123.24, 126.38) * mm});
            skLineSegment(sketch, "E30.27.62.0", {"start": v(124.49, 130.16) * mm, "end": v(124.98, 131.13) * mm});
            skLineSegment(sketch, "E30.30.62.0", {"start": v(124.96, 121.56) * mm, "end": v(124.8, 121.73) * mm});
            skLineSegment(sketch, "E30.33.62.0", {"start": v(124.63, 121.9) * mm, "end": v(124.8, 121.73) * mm});
            skArc(sketch, "E30.1.63.0", {"start": v(112.9, 141.66) * mm, "mid": v(113.3, 143.09) * mm, "end": v(113.37, 144.57) * mm});
            skArc(sketch, "E30.4.63.0", {"start": v(122.9, 133.1) * mm, "mid": v(124.26, 133.7) * mm, "end": v(125.71, 134) * mm});
            skLineSegment(sketch, "E30.8.63.0", {"start": v(121.97, 132.54) * mm, "end": v(122.9, 133.1) * mm});
            skArc(sketch, "E30.11.63.0", {"start": v(121.97, 132.54) * mm, "mid": v(120.2, 131.65) * mm, "end": v(118.3, 131.04) * mm});
            skArc(sketch, "E30.15.63.0", {"start": v(118.3, 131.04) * mm, "mid": v(115.88, 131.03) * mm, "end": v(113.73, 132.13) * mm});
            skArc(sketch, "E30.19.63.0", {"start": v(111.58, 136.78) * mm, "mid": v(111.95, 134.4) * mm, "end": v(113.37, 132.44) * mm});
            skArc(sketch, "E30.23.63.0", {"start": v(112.5, 140.65) * mm, "mid": v(111.9, 138.75) * mm, "end": v(111.58, 136.78) * mm});
            skLineSegment(sketch, "E30.27.63.0", {"start": v(112.5, 140.65) * mm, "end": v(112.9, 141.66) * mm});
            skLineSegment(sketch, "E30.30.63.0", {"start": v(113.73, 132.13) * mm, "end": v(113.55, 132.29) * mm});
            skLineSegment(sketch, "E30.33.63.0", {"start": v(113.37, 132.44) * mm, "end": v(113.55, 132.29) * mm});
            skArc(sketch, "E30.1.64.0", {"start": v(99.94, 151.08) * mm, "mid": v(100.21, 152.54) * mm, "end": v(100.15, 154.02) * mm});
            skArc(sketch, "E30.4.64.0", {"start": v(110.67, 143.44) * mm, "mid": v(111.96, 144.17) * mm, "end": v(113.38, 144.59) * mm});
            skLineSegment(sketch, "E30.8.64.0", {"start": v(109.78, 142.8) * mm, "end": v(110.67, 143.44) * mm});
            skArc(sketch, "E30.11.64.0", {"start": v(109.78, 142.8) * mm, "mid": v(108.09, 141.76) * mm, "end": v(106.25, 140.98) * mm});
            skArc(sketch, "E30.15.64.0", {"start": v(106.25, 140.98) * mm, "mid": v(103.85, 140.76) * mm, "end": v(101.6, 141.67) * mm});
            skArc(sketch, "E30.19.64.0", {"start": v(99.06, 146.1) * mm, "mid": v(99.64, 143.76) * mm, "end": v(101.22, 141.94) * mm});
            skArc(sketch, "E30.23.64.0", {"start": v(99.63, 150.04) * mm, "mid": v(99.2, 148.1) * mm, "end": v(99.06, 146.1) * mm});
            skLineSegment(sketch, "E30.27.64.0", {"start": v(99.63, 150.04) * mm, "end": v(99.94, 151.08) * mm});
            skLineSegment(sketch, "E30.30.64.0", {"start": v(101.6, 141.67) * mm, "end": v(101.41, 141.8) * mm});
            skLineSegment(sketch, "E30.33.64.0", {"start": v(101.22, 141.94) * mm, "end": v(101.41, 141.8) * mm});
            skArc(sketch, "E30.1.65.0", {"start": v(86.2, 159.32) * mm, "mid": v(86.34, 160.8) * mm, "end": v(86.14, 162.27) * mm});
            skArc(sketch, "E30.4.65.0", {"start": v(97.55, 152.66) * mm, "mid": v(98.78, 153.5) * mm, "end": v(100.16, 154.04) * mm});
            skLineSegment(sketch, "E30.8.65.0", {"start": v(96.73, 151.94) * mm, "end": v(97.55, 152.66) * mm});
            skArc(sketch, "E30.11.65.0", {"start": v(96.73, 151.94) * mm, "mid": v(95.13, 150.75) * mm, "end": v(93.37, 149.82) * mm});
            skArc(sketch, "E30.15.65.0", {"start": v(93.37, 149.82) * mm, "mid": v(91, 149.4) * mm, "end": v(88.69, 150.1) * mm});
            skArc(sketch, "E30.19.65.0", {"start": v(85.76, 154.3) * mm, "mid": v(86.54, 152) * mm, "end": v(88.28, 150.33) * mm});
            skArc(sketch, "E30.23.65.0", {"start": v(85.98, 158.26) * mm, "mid": v(85.72, 156.28) * mm, "end": v(85.76, 154.3) * mm});
            skLineSegment(sketch, "E30.27.65.0", {"start": v(85.98, 158.26) * mm, "end": v(86.2, 159.32) * mm});
            skLineSegment(sketch, "E30.30.65.0", {"start": v(88.69, 150.1) * mm, "end": v(88.48, 150.21) * mm});
            skLineSegment(sketch, "E30.33.65.0", {"start": v(88.28, 150.33) * mm, "end": v(88.48, 150.21) * mm});
            skArc(sketch, "E30.1.66.0", {"start": v(71.78, 166.32) * mm, "mid": v(71.79, 167.8) * mm, "end": v(71.46, 169.25) * mm});
            skArc(sketch, "E30.4.66.0", {"start": v(83.68, 160.68) * mm, "mid": v(84.83, 161.63) * mm, "end": v(86.15, 162.3) * mm});
            skLineSegment(sketch, "E30.8.66.0", {"start": v(82.93, 159.9) * mm, "end": v(83.68, 160.68) * mm});
            skArc(sketch, "E30.11.66.0", {"start": v(82.93, 159.9) * mm, "mid": v(81.44, 158.57) * mm, "end": v(79.77, 157.48) * mm});
            skArc(sketch, "E30.15.66.0", {"start": v(79.77, 157.48) * mm, "mid": v(77.44, 156.85) * mm, "end": v(75.08, 157.34) * mm});
            skArc(sketch, "E30.19.66.0", {"start": v(71.79, 161.27) * mm, "mid": v(72.77, 159.06) * mm, "end": v(74.65, 157.55) * mm});
            skArc(sketch, "E30.23.66.0", {"start": v(71.65, 165.24) * mm, "mid": v(71.57, 163.25) * mm, "end": v(71.79, 161.27) * mm});
            skLineSegment(sketch, "E30.27.66.0", {"start": v(71.65, 165.24) * mm, "end": v(71.78, 166.32) * mm});
            skLineSegment(sketch, "E30.30.66.0", {"start": v(75.08, 157.34) * mm, "end": v(74.86, 157.44) * mm});
            skLineSegment(sketch, "E30.33.66.0", {"start": v(74.65, 157.55) * mm, "end": v(74.86, 157.44) * mm});
            skArc(sketch, "E30.1.67.0", {"start": v(56.8, 172.01) * mm, "mid": v(56.68, 173.5) * mm, "end": v(56.22, 174.9) * mm});
            skArc(sketch, "E30.4.67.0", {"start": v(69.15, 167.45) * mm, "mid": v(70.2, 168.5) * mm, "end": v(71.47, 169.27) * mm});
            skLineSegment(sketch, "E30.8.67.0", {"start": v(68.47, 166.6) * mm, "end": v(69.15, 167.45) * mm});
            skArc(sketch, "E30.11.67.0", {"start": v(68.47, 166.6) * mm, "mid": v(67.1, 165.15) * mm, "end": v(65.54, 163.92) * mm});
            skArc(sketch, "E30.15.67.0", {"start": v(65.54, 163.92) * mm, "mid": v(63.27, 163.08) * mm, "end": v(60.88, 163.36) * mm});
            skArc(sketch, "E30.19.67.0", {"start": v(57.25, 166.98) * mm, "mid": v(58.43, 164.87) * mm, "end": v(60.43, 163.53) * mm});
            skArc(sketch, "E30.23.67.0", {"start": v(56.77, 170.93) * mm, "mid": v(56.86, 168.93) * mm, "end": v(57.25, 166.98) * mm});
            skLineSegment(sketch, "E30.27.67.0", {"start": v(56.77, 170.93) * mm, "end": v(56.8, 172.01) * mm});
            skLineSegment(sketch, "E30.30.67.0", {"start": v(60.88, 163.36) * mm, "end": v(60.65, 163.44) * mm});
            skLineSegment(sketch, "E30.33.67.0", {"start": v(60.43, 163.53) * mm, "end": v(60.65, 163.44) * mm});
            skArc(sketch, "E30.1.68.0", {"start": v(41.38, 176.36) * mm, "mid": v(41.12, 177.82) * mm, "end": v(40.55, 179.19) * mm});
            skArc(sketch, "E30.4.68.0", {"start": v(54.08, 172.9) * mm, "mid": v(55.04, 174.04) * mm, "end": v(56.23, 174.92) * mm});
            skLineSegment(sketch, "E30.8.68.0", {"start": v(53.48, 172) * mm, "end": v(54.08, 172.9) * mm});
            skArc(sketch, "E30.11.68.0", {"start": v(53.48, 172) * mm, "mid": v(52.25, 170.43) * mm, "end": v(50.8, 169.07) * mm});
            skArc(sketch, "E30.15.68.0", {"start": v(50.8, 169.07) * mm, "mid": v(48.61, 168.03) * mm, "end": v(46.2, 168.1) * mm});
            skArc(sketch, "E30.19.68.0", {"start": v(42.27, 171.39) * mm, "mid": v(43.63, 169.39) * mm, "end": v(45.74, 168.23) * mm});
            skArc(sketch, "E30.23.68.0", {"start": v(41.44, 175.27) * mm, "mid": v(41.7, 173.3) * mm, "end": v(42.27, 171.39) * mm});
            skLineSegment(sketch, "E30.27.68.0", {"start": v(41.44, 175.27) * mm, "end": v(41.38, 176.36) * mm});
            skLineSegment(sketch, "E30.30.68.0", {"start": v(46.2, 168.1) * mm, "end": v(45.97, 168.17) * mm});
            skLineSegment(sketch, "E30.33.68.0", {"start": v(45.74, 168.23) * mm, "end": v(45.97, 168.17) * mm});
            skArc(sketch, "E30.1.69.0", {"start": v(25.63, 179.33) * mm, "mid": v(25.25, 180.76) * mm, "end": v(24.55, 182.07) * mm});
            skArc(sketch, "E30.4.69.0", {"start": v(38.6, 177) * mm, "mid": v(39.45, 178.22) * mm, "end": v(40.55, 179.2) * mm});
            skLineSegment(sketch, "E30.8.69.0", {"start": v(38.07, 176.05) * mm, "end": v(38.6, 177) * mm});
            skArc(sketch, "E30.11.69.0", {"start": v(38.07, 176.05) * mm, "mid": v(36.98, 174.38) * mm, "end": v(35.65, 172.9) * mm});
            skArc(sketch, "E30.15.69.0", {"start": v(35.65, 172.9) * mm, "mid": v(33.57, 171.67) * mm, "end": v(31.16, 171.53) * mm});
            skArc(sketch, "E30.19.69.0", {"start": v(26.96, 174.45) * mm, "mid": v(28.48, 172.58) * mm, "end": v(30.7, 171.61) * mm});
            skArc(sketch, "E30.23.69.0", {"start": v(25.79, 178.25) * mm, "mid": v(26.23, 176.3) * mm, "end": v(26.96, 174.45) * mm});
            skLineSegment(sketch, "E30.27.69.0", {"start": v(25.79, 178.25) * mm, "end": v(25.63, 179.33) * mm});
            skLineSegment(sketch, "E30.30.69.0", {"start": v(31.16, 171.53) * mm, "end": v(30.93, 171.57) * mm});
            skLineSegment(sketch, "E30.33.69.0", {"start": v(30.7, 171.61) * mm, "end": v(30.93, 171.57) * mm});
            skArc(sketch, "E30.1.70.0", {"start": v(9.68, 180.89) * mm, "mid": v(9.17, 182.28) * mm, "end": v(8.36, 183.53) * mm});
            skArc(sketch, "E30.4.70.0", {"start": v(22.8, 179.73) * mm, "mid": v(23.54, 181) * mm, "end": v(24.55, 182.1) * mm});
            skLineSegment(sketch, "E30.8.70.0", {"start": v(22.36, 178.73) * mm, "end": v(22.8, 179.73) * mm});
            skArc(sketch, "E30.11.70.0", {"start": v(22.36, 178.73) * mm, "mid": v(21.42, 176.97) * mm, "end": v(20.23, 175.37) * mm});
            skArc(sketch, "E30.15.70.0", {"start": v(20.23, 175.37) * mm, "mid": v(18.27, 173.97) * mm, "end": v(15.88, 173.61) * mm});
            skArc(sketch, "E30.19.70.0", {"start": v(11.43, 176.15) * mm, "mid": v(13.12, 174.42) * mm, "end": v(15.4, 173.65) * mm});
            skArc(sketch, "E30.23.70.0", {"start": v(9.93, 179.83) * mm, "mid": v(10.55, 177.94) * mm, "end": v(11.43, 176.15) * mm});
            skLineSegment(sketch, "E30.27.70.0", {"start": v(9.93, 179.83) * mm, "end": v(9.68, 180.89) * mm});
            skLineSegment(sketch, "E30.30.70.0", {"start": v(15.88, 173.61) * mm, "end": v(15.64, 173.63) * mm});
            skLineSegment(sketch, "E30.33.70.0", {"start": v(15.4, 173.65) * mm, "end": v(15.64, 173.63) * mm});
            skSolve(sketch);
        }
        {
            var Q0;
            {var subQ171=sQuery(id+"F2.wireOp",EDGE,"E15");Q0=makeQuery(id+"F2.imprint","IMPRINT",FACE,{"disambiguationData":[TD([[makeQuery(id+"F2.imprint","IMPRINT",EDGE,{"derivedFrom":subQ171}),1.0]])]});}
            extrude(context, id + "F3", {"entities" : qUnion([Q0]), "operationType" : NewBodyOperationType.INTERSECT, "endBound" : BoundingType.THROUGH_ALL, "oppositeDirection" : true, "depth" : 25 * mm, "offsetDistance" : 25 * mm});
        }
        {
            var Q0;
            Q0=qCreatedBy(makeId("Right.planeOp"),FACE);
            var sketch = newSketch(context, id + "F4", { "sketchPlane" : qUnion([Q0])});
            skLineSegment(sketch, "E31", {"start": v(0, 72.2) * mm, "end": v(0, -78.72) * mm, "construction": true});
            skLineSegment(sketch, "E32", {"start": v(-84.45, 0) * mm, "end": v(97.88, 0) * mm, "construction": true});
            skCircle(sketch, "E33", {"center": v(0, 0) * mm, "radius": 52 * mm, "construction": true});
            skCircle(sketch, "E34", {"center": v(0, 52) * mm, "radius": 5.25 * mm});
            skCircle(sketch, "E35.1.0", {"center": v(-45.03, 26) * mm, "radius": 5.25 * mm});
            skCircle(sketch, "E35.2.0", {"center": v(-45.03, -26) * mm, "radius": 5.25 * mm});
            skCircle(sketch, "E35.3.0", {"center": v(0, -52) * mm, "radius": 5.25 * mm});
            skCircle(sketch, "E35.4.0", {"center": v(45.03, -26) * mm, "radius": 5.25 * mm});
            skCircle(sketch, "E35.5.0", {"center": v(45.03, 26) * mm, "radius": 5.25 * mm});
            skSolve(sketch);
        }
        {
            var Q0;
            Q0=makeQuery(id+"F4.imprint","IMPRINT",FACE,{"disambiguationData":[TD([[makeQuery(id+"F4.imprint","IMPRINT",EDGE,{"derivedFrom":sQuery(id+"F4.wireOp",EDGE,"E35.5.0")}),1.0]])]});
            var Q1;
            Q1=makeQuery(id+"F4.imprint","IMPRINT",FACE,{"disambiguationData":[TD([[makeQuery(id+"F4.imprint","IMPRINT",EDGE,{"derivedFrom":sQuery(id+"F4.wireOp",EDGE,"E34")}),1.0]])]});
            var Q2;
            Q2=makeQuery(id+"F4.imprint","IMPRINT",FACE,{"disambiguationData":[TD([[makeQuery(id+"F4.imprint","IMPRINT",EDGE,{"derivedFrom":sQuery(id+"F4.wireOp",EDGE,"E35.4.0")}),1.0]])]});
            var Q3;
            Q3=makeQuery(id+"F4.imprint","IMPRINT",FACE,{"disambiguationData":[TD([[makeQuery(id+"F4.imprint","IMPRINT",EDGE,{"derivedFrom":sQuery(id+"F4.wireOp",EDGE,"E35.3.0")}),1.0]])]});
            var Q4;
            Q4=makeQuery(id+"F4.imprint","IMPRINT",FACE,{"disambiguationData":[TD([[makeQuery(id+"F4.imprint","IMPRINT",EDGE,{"derivedFrom":sQuery(id+"F4.wireOp",EDGE,"E35.2.0")}),1.0]])]});
            var Q5;
            Q5=makeQuery(id+"F4.imprint","IMPRINT",FACE,{"disambiguationData":[TD([[makeQuery(id+"F4.imprint","IMPRINT",EDGE,{"derivedFrom":sQuery(id+"F4.wireOp",EDGE,"E35.1.0")}),1.0]])]});
            var Q6;
            Q6=sQuery(id+"F4.wireOp",EDGE,"E35.1.0");
            var Q7;
            Q7=sQuery(id+"F4.wireOp",EDGE,"E34");
            var Q8;
            Q8=sQuery(id+"F4.wireOp",EDGE,"E35.5.0");
            var Q9;
            Q9=sQuery(id+"F4.wireOp",EDGE,"E35.4.0");
            var Q10;
            Q10=sQuery(id+"F4.wireOp",EDGE,"E35.3.0");
            var Q11;
            Q11=sQuery(id+"F4.wireOp",EDGE,"E35.2.0");
            extrude(context, id + "F5", {"entities" : qUnion([Q0, Q1, Q2, Q3, Q4, Q5]), "operationType" : NewBodyOperationType.REMOVE, "surfaceEntities" : qUnion([Q6, Q7, Q8, Q9, Q10, Q11]), "depth" : 25 * mm, "offsetDistance" : 25 * mm});
        }
        {
            var Q0;
            Q0=makeQuery(id+"F1.opRevolve","SWEPT_FACE",FACE,{"disambiguationData":[OSD([sQuery(id+"F0.wireOp",EDGE,"E1.right")])]});
            var Q1;
            Q1=makeQuery(id+"F1.opRevolve","SWEPT_FACE",FACE,{"disambiguationData":[OSD([sQuery(id+"F0.wireOp",EDGE,"E1.left")])]});
            chamfer(context, id + "F6", {"entities" : qUnion([Q0, Q1]), "width" : 1 * mm, "tangentPropagation" : true});
        }
    });
